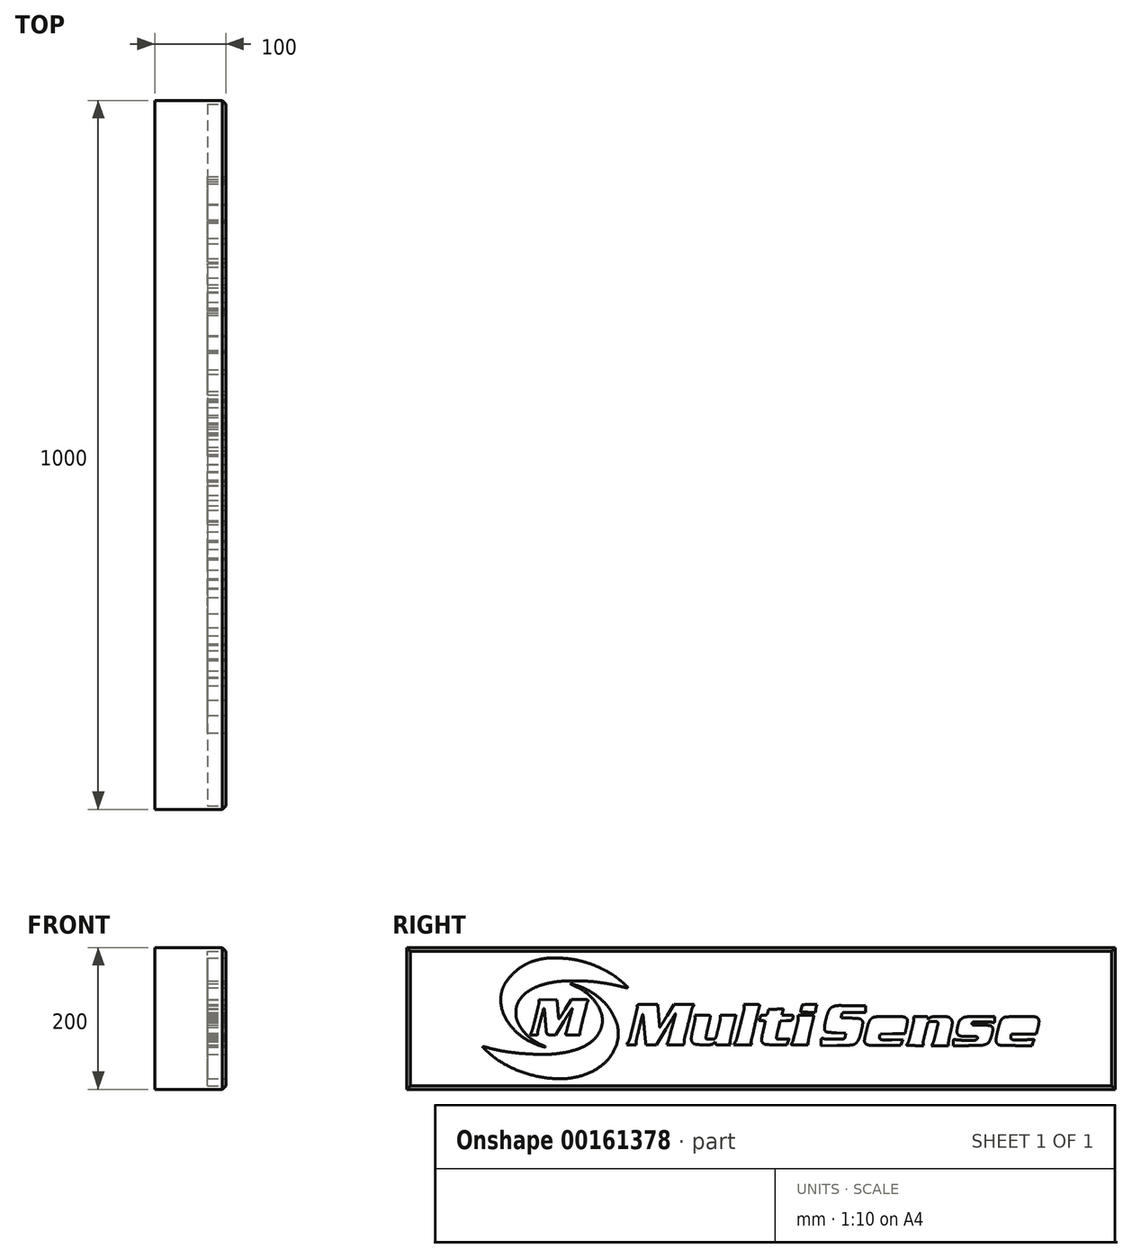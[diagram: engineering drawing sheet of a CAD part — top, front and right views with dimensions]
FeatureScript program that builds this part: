
annotation { "Feature Type Name" : "Feature", "Feature Type Description" : "" }
export const myFeature = defineFeature(function(context is Context, id is Id, definition is map)
    precondition{}
    {
        {
            var Q0;
            Q0=qCreatedBy(makeId("Right.planeOp"),FACE);
            var sketch = newSketch(context, id + "F0", { "sketchPlane" : qUnion([Q0])});
            skLineSegment(sketch, "E0.bottom", {"start": v(500, 100) * mm, "end": v(-500, 100) * mm});
            skLineSegment(sketch, "E0.top", {"start": v(500, -100) * mm, "end": v(-500, -100) * mm});
            skLineSegment(sketch, "E0.left", {"start": v(500, 100) * mm, "end": v(500, -100) * mm});
            skLineSegment(sketch, "E0.right", {"start": v(-500, 100) * mm, "end": v(-500, -100) * mm});
            skPoint(sketch, "E0.middle", {"position": v(0, 0) * mm});
            skSolve(sketch);
        }
        {
            var Q0;
            Q0=makeQuery(id+"F0.imprint","IMPRINT",FACE,{"disambiguationData":[TD([[makeQuery(id+"F0.imprint","IMPRINT",EDGE,{"derivedFrom":sQuery(id+"F0.wireOp",EDGE,"0kaTTqBf-60IO-ZrBU-QRsl-RT9rZZWctxwf")}),1.0]])]});
            var Q1;
            Q1=makeQuery(id+"F0.imprint","IMPRINT",FACE,{"disambiguationData":[TD([[makeQuery(id+"F0.imprint","IMPRINT",EDGE,{"derivedFrom":sQuery(id+"F0.wireOp",EDGE,"E0.bottom")}),1.0]])]});
            extrude(context, id + "F1", {"entities" : qUnion([Q0, Q1]), "depth" : 100 * mm});
        }
        {
            var Q0;
            Q0=makeQuery(id+"F1.opExtrude","CAP_EDGE",EDGE,{"disambiguationData":[OSD([sQuery(id+"F0.wireOp",EDGE,"E0.bottom")])],"isStart":false});
            var Q1;
            Q1=makeQuery(id+"F1.opExtrude","CAP_EDGE",EDGE,{"disambiguationData":[OSD([sQuery(id+"F0.wireOp",EDGE,"E0.right")])],"isStart":false});
            var Q2;
            Q2=makeQuery(id+"F1.opExtrude","CAP_EDGE",EDGE,{"disambiguationData":[OSD([sQuery(id+"F0.wireOp",EDGE,"E0.top")])],"isStart":false});
            var Q3;
            Q3=makeQuery(id+"F1.opExtrude","CAP_EDGE",EDGE,{"disambiguationData":[OSD([sQuery(id+"F0.wireOp",EDGE,"E0.left")])],"isStart":false});
            chamfer(context, id + "F2", {"entities" : qUnion([Q0, Q1, Q2, Q3]), "width" : 5 * mm, "tangentPropagation" : true});
        }
        {
            var Q0;
            Q0=makeQuery(id+"F1.opExtrude","CAP_FACE",FACE,{"disambiguationData":[OSD([sQuery(id+"F0.wireOp",EDGE,"E0.bottom"),sQuery(id+"F0.wireOp",EDGE,"E0.top"),sQuery(id+"F0.wireOp",EDGE,"E0.left"),sQuery(id+"F0.wireOp",EDGE,"E0.right")])],"isStart":false});
            var sketch = newSketch(context, id + "F3", { "sketchPlane" : qUnion([Q0])});
            skArc(sketch, "E1", {"start": v(-307.52, 84.22) * mm, "mid": v(-314, 82.86) * mm, "end": v(-320.37, 81.12) * mm});
            skArc(sketch, "E2", {"start": v(-320.37, 81.12) * mm, "mid": v(-325.97, 79.14) * mm, "end": v(-331.38, 76.7) * mm});
            skArc(sketch, "E3", {"start": v(-331.38, 76.7) * mm, "mid": v(-336.4, 73.9) * mm, "end": v(-341.16, 70.67) * mm});
            skArc(sketch, "E4", {"start": v(-341.16, 70.67) * mm, "mid": v(-345.91, 66.85) * mm, "end": v(-350.37, 62.7) * mm});
            skArc(sketch, "E5", {"start": v(-350.37, 62.7) * mm, "mid": v(-354.46, 58.31) * mm, "end": v(-358.25, 53.66) * mm});
            skArc(sketch, "E6", {"start": v(-358.25, 53.66) * mm, "mid": v(-361.09, 49.48) * mm, "end": v(-363.45, 45.02) * mm});
            skArc(sketch, "E7", {"start": v(-363.45, 45.02) * mm, "mid": v(-365.18, 40.59) * mm, "end": v(-366.36, 35.99) * mm});
            skArc(sketch, "E8", {"start": v(-366.36, 35.99) * mm, "mid": v(-367.1, 30.93) * mm, "end": v(-367.34, 25.82) * mm});
            skArc(sketch, "E9", {"start": v(-367.34, 25.82) * mm, "mid": v(-366.34, 15.86) * mm, "end": v(-363.36, 6.3) * mm});
            skArc(sketch, "E10", {"start": v(-363.36, 6.3) * mm, "mid": v(-358.3, -3.45) * mm, "end": v(-351.8, -12.3) * mm});
            skArc(sketch, "E11", {"start": v(-351.8, -12.3) * mm, "mid": v(-343.53, -20.68) * mm, "end": v(-334.15, -27.8) * mm});
            skArc(sketch, "E12", {"start": v(-334.15, -27.8) * mm, "mid": v(-323.61, -33.75) * mm, "end": v(-312.4, -38.27) * mm});
            skArc(sketch, "E13", {"start": v(-312.4, -38.27) * mm, "mid": v(-309.3, -39.26) * mm, "end": v(-306.21, -40.23) * mm});
            skArc(sketch, "E14", {"start": v(-306.21, -40.23) * mm, "mid": v(-305.4, -40.35) * mm, "end": v(-304.6, -40.24) * mm});
            skArc(sketch, "E15", {"start": v(-304.6, -40.24) * mm, "mid": v(-304.38, -39.97) * mm, "end": v(-304.56, -39.66) * mm});
            skArc(sketch, "E16", {"start": v(-304.56, -39.66) * mm, "mid": v(-307.06, -38.53) * mm, "end": v(-309.58, -37.43) * mm});
            skArc(sketch, "E17", {"start": v(-309.58, -37.43) * mm, "mid": v(-314.83, -34.92) * mm, "end": v(-319.85, -31.98) * mm});
            skArc(sketch, "E18", {"start": v(-319.85, -31.98) * mm, "mid": v(-324.6, -28.62) * mm, "end": v(-329.03, -24.87) * mm});
            skArc(sketch, "E19", {"start": v(-329.03, -24.87) * mm, "mid": v(-333.02, -20.86) * mm, "end": v(-336.64, -16.52) * mm});
            skArc(sketch, "E20", {"start": v(-336.64, -16.52) * mm, "mid": v(-339.67, -12.08) * mm, "end": v(-342.24, -7.36) * mm});
            skArc(sketch, "E21", {"start": v(-342.24, -7.36) * mm, "mid": v(-343.26, -5.14) * mm, "end": v(-344.23, -2.9) * mm});
            skArc(sketch, "E22", {"start": v(-344.23, -2.9) * mm, "mid": v(-344.8, -1.36) * mm, "end": v(-345.23, 0.22) * mm});
            skArc(sketch, "E23", {"start": v(-345.23, 0.22) * mm, "mid": v(-345.52, 1.81) * mm, "end": v(-345.68, 3.42) * mm});
            skArc(sketch, "E24", {"start": v(-345.68, 3.42) * mm, "mid": v(-345.78, 5.78) * mm, "end": v(-345.8, 8.14) * mm});
            skArc(sketch, "E25", {"start": v(-345.8, 8.14) * mm, "mid": v(-345.77, 10.33) * mm, "end": v(-345.68, 12.52) * mm});
            skArc(sketch, "E26", {"start": v(-345.68, 12.52) * mm, "mid": v(-345.53, 14.12) * mm, "end": v(-345.27, 15.7) * mm});
            skArc(sketch, "E27", {"start": v(-345.27, 15.7) * mm, "mid": v(-344.93, 17.16) * mm, "end": v(-344.48, 18.58) * mm});
            skArc(sketch, "E28", {"start": v(-344.48, 18.58) * mm, "mid": v(-343.83, 20.26) * mm, "end": v(-343.11, 21.9) * mm});
            skArc(sketch, "E29", {"start": v(-343.11, 21.9) * mm, "mid": v(-339.85, 27.54) * mm, "end": v(-335.6, 32.48) * mm});
            skArc(sketch, "E30", {"start": v(-335.6, 32.48) * mm, "mid": v(-330.08, 37.17) * mm, "end": v(-323.98, 41.1) * mm});
            skArc(sketch, "E31", {"start": v(-323.98, 41.1) * mm, "mid": v(-316.38, 44.76) * mm, "end": v(-308.41, 47.56) * mm});
            skArc(sketch, "E32", {"start": v(-308.41, 47.56) * mm, "mid": v(-298.85, 49.98) * mm, "end": v(-289.15, 51.72) * mm});
            skArc(sketch, "E33", {"start": v(-289.15, 51.72) * mm, "mid": v(-284.13, 52.3) * mm, "end": v(-279.1, 52.6) * mm});
            skArc(sketch, "E34", {"start": v(-279.1, 52.6) * mm, "mid": v(-271.29, 52.8) * mm, "end": v(-263.49, 52.86) * mm});
            skArc(sketch, "E35", {"start": v(-263.49, 52.86) * mm, "mid": v(-255.52, 52.8) * mm, "end": v(-247.55, 52.6) * mm});
            skArc(sketch, "E36", {"start": v(-247.55, 52.6) * mm, "mid": v(-241.69, 52.3) * mm, "end": v(-235.84, 51.75) * mm});
            skArc(sketch, "E37", {"start": v(-235.84, 51.75) * mm, "mid": v(-230.71, 51.13) * mm, "end": v(-225.6, 50.44) * mm});
            skArc(sketch, "E38", {"start": v(-225.6, 50.44) * mm, "mid": v(-220.73, 49.7) * mm, "end": v(-215.88, 48.9) * mm});
            skArc(sketch, "E39", {"start": v(-215.88, 48.9) * mm, "mid": v(-211.3, 48.06) * mm, "end": v(-206.75, 47.14) * mm});
            skArc(sketch, "E40", {"start": v(-206.75, 47.14) * mm, "mid": v(-202.48, 46.2) * mm, "end": v(-198.24, 45.16) * mm});
            skArc(sketch, "E41", {"start": v(-198.24, 45.16) * mm, "mid": v(-196.43, 44.72) * mm, "end": v(-194.61, 44.29) * mm});
            skArc(sketch, "E42", {"start": v(-194.61, 44.29) * mm, "mid": v(-193.05, 43.94) * mm, "end": v(-191.48, 43.62) * mm});
            skArc(sketch, "E43", {"start": v(-191.48, 43.62) * mm, "mid": v(-190.15, 43.36) * mm, "end": v(-188.82, 43.1) * mm});
            skArc(sketch, "E44", {"start": v(-188.82, 43.1) * mm, "mid": v(-188.6, 43.12) * mm, "end": v(-188.42, 43.23) * mm});
            skArc(sketch, "E45", {"start": v(-188.42, 43.23) * mm, "mid": v(-188.16, 43.87) * mm, "end": v(-188.44, 44.5) * mm});
            skArc(sketch, "E46", {"start": v(-188.44, 44.5) * mm, "mid": v(-191.8, 47.56) * mm, "end": v(-195.19, 50.58) * mm});
            skArc(sketch, "E47", {"start": v(-195.19, 50.58) * mm, "mid": v(-198.7, 53.6) * mm, "end": v(-202.29, 56.52) * mm});
            skArc(sketch, "E48", {"start": v(-202.29, 56.52) * mm, "mid": v(-205.37, 58.84) * mm, "end": v(-208.55, 61.01) * mm});
            skArc(sketch, "E49", {"start": v(-208.55, 61.01) * mm, "mid": v(-214.74, 64.83) * mm, "end": v(-221.1, 68.34) * mm});
            skArc(sketch, "E50", {"start": v(-221.1, 68.34) * mm, "mid": v(-227.55, 71.52) * mm, "end": v(-234.15, 74.38) * mm});
            skArc(sketch, "E51", {"start": v(-234.15, 74.38) * mm, "mid": v(-240.93, 76.94) * mm, "end": v(-247.82, 79.16) * mm});
            skArc(sketch, "E52", {"start": v(-247.82, 79.16) * mm, "mid": v(-254.97, 81.1) * mm, "end": v(-262.2, 82.72) * mm});
            skArc(sketch, "E53", {"start": v(-262.2, 82.72) * mm, "mid": v(-267.5, 83.65) * mm, "end": v(-272.86, 84.29) * mm});
            skArc(sketch, "E54", {"start": v(-272.86, 84.29) * mm, "mid": v(-279.34, 84.8) * mm, "end": v(-285.83, 85.1) * mm});
            skArc(sketch, "E55", {"start": v(-285.83, 85.1) * mm, "mid": v(-292.1, 85.22) * mm, "end": v(-298.39, 85.14) * mm});
            skArc(sketch, "E56", {"start": v(-298.39, 85.14) * mm, "mid": v(-302.97, 84.85) * mm, "end": v(-307.52, 84.22) * mm});
            skArc(sketch, "E57", {"start": v(-264.04, 46.2) * mm, "mid": v(-255, 41.77) * mm, "end": v(-246.62, 36.19) * mm});
            skArc(sketch, "E58", {"start": v(-246.62, 36.19) * mm, "mid": v(-239.35, 29.72) * mm, "end": v(-233.1, 22.27) * mm});
            skArc(sketch, "E59", {"start": v(-233.1, 22.27) * mm, "mid": v(-228.54, 14.74) * mm, "end": v(-225.26, 6.56) * mm});
            skArc(sketch, "E60", {"start": v(-225.26, 6.56) * mm, "mid": v(-223.9, -1) * mm, "end": v(-224.4, -8.69) * mm});
            skArc(sketch, "E61", {"start": v(-224.4, -8.69) * mm, "mid": v(-226.65, -16.2) * mm, "end": v(-230.41, -23.1) * mm});
            skArc(sketch, "E62", {"start": v(-230.41, -23.1) * mm, "mid": v(-235.7, -29.47) * mm, "end": v(-242.05, -34.8) * mm});
            skArc(sketch, "E63", {"start": v(-242.05, -34.8) * mm, "mid": v(-250.38, -39.77) * mm, "end": v(-259.33, -43.47) * mm});
            skArc(sketch, "E64", {"start": v(-259.33, -43.47) * mm, "mid": v(-270.52, -46.66) * mm, "end": v(-281.95, -48.9) * mm});
            skArc(sketch, "E65", {"start": v(-281.95, -48.9) * mm, "mid": v(-293.44, -50.22) * mm, "end": v(-305, -50.7) * mm});
            skArc(sketch, "E66", {"start": v(-305, -50.7) * mm, "mid": v(-319.29, -50.5) * mm, "end": v(-333.55, -49.74) * mm});
            skArc(sketch, "E67", {"start": v(-333.55, -49.74) * mm, "mid": v(-347.86, -48.4) * mm, "end": v(-362.12, -46.52) * mm});
            skArc(sketch, "E68", {"start": v(-362.12, -46.52) * mm, "mid": v(-373.8, -44.33) * mm, "end": v(-385.3, -41.35) * mm});
            skArc(sketch, "E69", {"start": v(-385.3, -41.35) * mm, "mid": v(-386.55, -40.99) * mm, "end": v(-387.8, -40.65) * mm});
            skArc(sketch, "E70", {"start": v(-387.8, -40.65) * mm, "mid": v(-388.9, -40.38) * mm, "end": v(-390, -40.14) * mm});
            skArc(sketch, "E71", {"start": v(-390, -40.14) * mm, "mid": v(-390.91, -39.96) * mm, "end": v(-391.83, -39.8) * mm});
            skArc(sketch, "E72", {"start": v(-391.83, -39.8) * mm, "mid": v(-392.06, -39.82) * mm, "end": v(-392.25, -39.93) * mm});
            skArc(sketch, "E73", {"start": v(-392.25, -39.93) * mm, "mid": v(-392.5, -40.54) * mm, "end": v(-392.23, -41.13) * mm});
            skArc(sketch, "E74", {"start": v(-392.23, -41.13) * mm, "mid": v(-388.73, -44.37) * mm, "end": v(-385.2, -47.58) * mm});
            skArc(sketch, "E75", {"start": v(-385.2, -47.58) * mm, "mid": v(-381.63, -50.73) * mm, "end": v(-377.98, -53.8) * mm});
            skArc(sketch, "E76", {"start": v(-377.98, -53.8) * mm, "mid": v(-374.96, -56.15) * mm, "end": v(-371.83, -58.37) * mm});
            skArc(sketch, "E77", {"start": v(-371.83, -58.37) * mm, "mid": v(-358.73, -66.27) * mm, "end": v(-344.89, -72.78) * mm});
            skArc(sketch, "E78", {"start": v(-344.89, -72.78) * mm, "mid": v(-330.02, -78.08) * mm, "end": v(-314.71, -81.97) * mm});
            skArc(sketch, "E79", {"start": v(-314.71, -81.97) * mm, "mid": v(-299.63, -84.32) * mm, "end": v(-284.4, -85.21) * mm});
            skArc(sketch, "E80", {"start": v(-284.4, -85.21) * mm, "mid": v(-270.61, -84.46) * mm, "end": v(-257.04, -81.94) * mm});
            skArc(sketch, "E81", {"start": v(-257.04, -81.94) * mm, "mid": v(-244.14, -77.62) * mm, "end": v(-232.02, -71.43) * mm});
            skArc(sketch, "E82", {"start": v(-232.02, -71.43) * mm, "mid": v(-221.84, -63.89) * mm, "end": v(-213.2, -54.6) * mm});
            skArc(sketch, "E83", {"start": v(-213.2, -54.6) * mm, "mid": v(-207.02, -44.64) * mm, "end": v(-202.98, -33.63) * mm});
            skArc(sketch, "E84", {"start": v(-202.98, -33.63) * mm, "mid": v(-201.43, -22.43) * mm, "end": v(-202.43, -11.16) * mm});
            skArc(sketch, "E85", {"start": v(-202.43, -11.16) * mm, "mid": v(-203.29, -7.77) * mm, "end": v(-204.46, -4.47) * mm});
            skArc(sketch, "E86", {"start": v(-204.46, -4.47) * mm, "mid": v(-206.3, -0.23) * mm, "end": v(-208.32, 3.92) * mm});
            skArc(sketch, "E87", {"start": v(-208.32, 3.92) * mm, "mid": v(-210.55, 8.08) * mm, "end": v(-212.96, 12.14) * mm});
            skArc(sketch, "E88", {"start": v(-212.96, 12.14) * mm, "mid": v(-215.12, 15.35) * mm, "end": v(-217.52, 18.39) * mm});
            skArc(sketch, "E89", {"start": v(-217.52, 18.39) * mm, "mid": v(-222, 23.25) * mm, "end": v(-226.81, 27.78) * mm});
            skArc(sketch, "E90", {"start": v(-226.81, 27.78) * mm, "mid": v(-231.98, 31.97) * mm, "end": v(-237.45, 35.77) * mm});
            skArc(sketch, "E91", {"start": v(-237.45, 35.77) * mm, "mid": v(-243.27, 39.23) * mm, "end": v(-249.33, 42.27) * mm});
            skArc(sketch, "E92", {"start": v(-249.33, 42.27) * mm, "mid": v(-255.76, 44.97) * mm, "end": v(-262.34, 47.23) * mm});
            skArc(sketch, "E93", {"start": v(-262.34, 47.23) * mm, "mid": v(-264.75, 47.96) * mm, "end": v(-267.17, 48.66) * mm});
            skArc(sketch, "E94", {"start": v(-267.17, 48.66) * mm, "mid": v(-267.72, 48.7) * mm, "end": v(-268.24, 48.52) * mm});
            skArc(sketch, "E95", {"start": v(-268.24, 48.52) * mm, "mid": v(-268.39, 48.24) * mm, "end": v(-268.2, 47.99) * mm});
            skArc(sketch, "E96", {"start": v(-268.2, 47.99) * mm, "mid": v(-266.13, 47.08) * mm, "end": v(-264.04, 46.2) * mm});
            skArc(sketch, "E97", {"start": v(-313.34, 23.63) * mm, "mid": v(-313.48, 21.37) * mm, "end": v(-313.87, 19.14) * mm});
            skArc(sketch, "E98", {"start": v(-313.87, 19.14) * mm, "mid": v(-315.82, 10.99) * mm, "end": v(-317.81, 2.84) * mm});
            skArc(sketch, "E99", {"start": v(-317.81, 2.84) * mm, "mid": v(-319.8, -5.08) * mm, "end": v(-321.82, -12.99) * mm});
            skArc(sketch, "E100", {"start": v(-321.82, -12.99) * mm, "mid": v(-322.75, -16.1) * mm, "end": v(-323.89, -19.12) * mm});
            skArc(sketch, "E101", {"start": v(-323.89, -19.12) * mm, "mid": v(-324.17, -19.8) * mm, "end": v(-324.45, -20.48) * mm});
            skArc(sketch, "E102", {"start": v(-324.45, -20.48) * mm, "mid": v(-324.68, -21.09) * mm, "end": v(-324.92, -21.7) * mm});
            skArc(sketch, "E103", {"start": v(-324.92, -21.7) * mm, "mid": v(-325.1, -22.2) * mm, "end": v(-325.3, -22.72) * mm});
            skArc(sketch, "E104", {"start": v(-325.3, -22.72) * mm, "mid": v(-325.33, -22.85) * mm, "end": v(-325.34, -22.98) * mm});
            skArc(sketch, "E105", {"start": v(-325.34, -22.98) * mm, "mid": v(-325.3, -23.09) * mm, "end": v(-325.2, -23.13) * mm});
            skArc(sketch, "E106", {"start": v(-325.2, -23.13) * mm, "mid": v(-324.49, -23.2) * mm, "end": v(-323.77, -23.25) * mm});
            skArc(sketch, "E107", {"start": v(-323.77, -23.25) * mm, "mid": v(-322.9, -23.3) * mm, "end": v(-322.04, -23.33) * mm});
            skArc(sketch, "E108", {"start": v(-322.04, -23.33) * mm, "mid": v(-321.01, -23.35) * mm, "end": v(-319.98, -23.36) * mm});
            skArc(sketch, "E109", {"start": v(-319.98, -23.36) * mm, "mid": v(-318.34, -23.35) * mm, "end": v(-316.7, -23.3) * mm});
            skArc(sketch, "E110", {"start": v(-316.7, -23.3) * mm, "mid": v(-316.08, -23.23) * mm, "end": v(-315.48, -23.02) * mm});
            skArc(sketch, "E111", {"start": v(-315.48, -23.02) * mm, "mid": v(-315.15, -22.76) * mm, "end": v(-314.99, -22.37) * mm});
            skArc(sketch, "E112", {"start": v(-314.99, -22.37) * mm, "mid": v(-314.94, -21.74) * mm, "end": v(-315, -21.11) * mm});
            skArc(sketch, "E113", {"start": v(-315, -21.11) * mm, "mid": v(-315.12, -19.27) * mm, "end": v(-314.86, -17.44) * mm});
            skArc(sketch, "E114", {"start": v(-314.86, -17.44) * mm, "mid": v(-312.92, -9.67) * mm, "end": v(-310.94, -1.9) * mm});
            skArc(sketch, "E115", {"start": v(-310.94, -1.9) * mm, "mid": v(-308.92, 5.86) * mm, "end": v(-306.86, 13.62) * mm});
            skArc(sketch, "E116", {"start": v(-306.86, 13.62) * mm, "mid": v(-306.45, 13.94) * mm, "end": v(-306.02, 13.64) * mm});
            skArc(sketch, "E117", {"start": v(-306.02, 13.64) * mm, "mid": v(-305.88, 13.1) * mm, "end": v(-305.79, 12.55) * mm});
            skArc(sketch, "E118", {"start": v(-305.79, 12.55) * mm, "mid": v(-305.56, 10.36) * mm, "end": v(-305.34, 8.17) * mm});
            skArc(sketch, "E119", {"start": v(-305.34, 8.17) * mm, "mid": v(-305.1, 5.59) * mm, "end": v(-304.86, 3) * mm});
            skArc(sketch, "E120", {"start": v(-304.86, 3) * mm, "mid": v(-304.62, 0.07) * mm, "end": v(-304.39, -2.86) * mm});
            skArc(sketch, "E121", {"start": v(-304.39, -2.86) * mm, "mid": v(-303.8, -10.36) * mm, "end": v(-303.18, -17.85) * mm});
            skArc(sketch, "E122", {"start": v(-303.18, -17.85) * mm, "mid": v(-302.9, -19.65) * mm, "end": v(-302.33, -21.4) * mm});
            skArc(sketch, "E123", {"start": v(-302.33, -21.4) * mm, "mid": v(-301.6, -22.39) * mm, "end": v(-300.47, -22.92) * mm});
            skArc(sketch, "E124", {"start": v(-300.47, -22.92) * mm, "mid": v(-298.26, -23.25) * mm, "end": v(-296.01, -23.35) * mm});
            skLineSegment(sketch, "E125", {"start": v(-296.01, -23.35) * mm, "end": v(-289.84, -23.35) * mm});
            skLineSegment(sketch, "E126", {"start": v(-289.84, -23.35) * mm, "end": v(-278.36, -4.32) * mm});
            skArc(sketch, "E127", {"start": v(-278.36, -4.32) * mm, "mid": v(-276.15, -0.7) * mm, "end": v(-273.93, 2.92) * mm});
            skArc(sketch, "E128", {"start": v(-273.93, 2.92) * mm, "mid": v(-272.06, 5.91) * mm, "end": v(-270.17, 8.89) * mm});
            skArc(sketch, "E129", {"start": v(-270.17, 8.89) * mm, "mid": v(-268.53, 11.43) * mm, "end": v(-266.9, 13.96) * mm});
            skArc(sketch, "E130", {"start": v(-266.9, 13.96) * mm, "mid": v(-266.74, 14.03) * mm, "end": v(-266.62, 13.92) * mm});
            skArc(sketch, "E131", {"start": v(-266.62, 13.92) * mm, "mid": v(-266.52, 13.29) * mm, "end": v(-266.59, 12.65) * mm});
            skArc(sketch, "E132", {"start": v(-266.59, 12.65) * mm, "mid": v(-268.61, 4.75) * mm, "end": v(-270.65, -3.15) * mm});
            skArc(sketch, "E133", {"start": v(-270.65, -3.15) * mm, "mid": v(-272.57, -10.57) * mm, "end": v(-274.51, -17.98) * mm});
            skArc(sketch, "E134", {"start": v(-274.51, -17.98) * mm, "mid": v(-275.08, -19.82) * mm, "end": v(-275.78, -21.61) * mm});
            skArc(sketch, "E135", {"start": v(-275.78, -21.61) * mm, "mid": v(-275.86, -22.08) * mm, "end": v(-275.68, -22.53) * mm});
            skArc(sketch, "E136", {"start": v(-275.68, -22.53) * mm, "mid": v(-275.29, -22.9) * mm, "end": v(-274.78, -23.09) * mm});
            skArc(sketch, "E137", {"start": v(-274.78, -23.09) * mm, "mid": v(-273.57, -23.25) * mm, "end": v(-272.35, -23.32) * mm});
            skArc(sketch, "E138", {"start": v(-272.35, -23.32) * mm, "mid": v(-269.15, -23.35) * mm, "end": v(-265.95, -23.36) * mm});
            skLineSegment(sketch, "E139", {"start": v(-265.95, -23.36) * mm, "end": v(-255.34, -23.36) * mm});
            skLineSegment(sketch, "E140", {"start": v(-255.34, -23.36) * mm, "end": v(-255.34, -20.32) * mm});
            skArc(sketch, "E141", {"start": v(-255.34, -20.32) * mm, "mid": v(-255.2, -17.9) * mm, "end": v(-254.77, -15.5) * mm});
            skArc(sketch, "E142", {"start": v(-254.77, -15.5) * mm, "mid": v(-252.55, -6.33) * mm, "end": v(-250.29, 2.83) * mm});
            skArc(sketch, "E143", {"start": v(-250.29, 2.83) * mm, "mid": v(-247.9, 12.4) * mm, "end": v(-245.48, 21.96) * mm});
            skArc(sketch, "E144", {"start": v(-245.48, 21.96) * mm, "mid": v(-245.02, 23.1) * mm, "end": v(-244.28, 24.09) * mm});
            skArc(sketch, "E145", {"start": v(-244.28, 24.09) * mm, "mid": v(-243.95, 24.66) * mm, "end": v(-243.92, 25.32) * mm});
            skArc(sketch, "E146", {"start": v(-243.92, 25.32) * mm, "mid": v(-244.22, 25.87) * mm, "end": v(-244.76, 26.17) * mm});
            skArc(sketch, "E147", {"start": v(-244.76, 26.17) * mm, "mid": v(-246.35, 26.45) * mm, "end": v(-247.96, 26.56) * mm});
            skArc(sketch, "E148", {"start": v(-247.96, 26.56) * mm, "mid": v(-251.78, 26.62) * mm, "end": v(-255.6, 26.64) * mm});
            skLineSegment(sketch, "E149", {"start": v(-255.6, 26.64) * mm, "end": v(-267.84, 26.63) * mm});
            skLineSegment(sketch, "E150", {"start": v(-267.84, 26.63) * mm, "end": v(-276.34, 12.74) * mm});
            skArc(sketch, "E151", {"start": v(-276.34, 12.74) * mm, "mid": v(-277.98, 10.08) * mm, "end": v(-279.63, 7.44) * mm});
            skArc(sketch, "E152", {"start": v(-279.63, 7.44) * mm, "mid": v(-281.04, 5.23) * mm, "end": v(-282.47, 3.04) * mm});
            skArc(sketch, "E153", {"start": v(-282.47, 3.04) * mm, "mid": v(-283.72, 1.17) * mm, "end": v(-284.98, -0.71) * mm});
            skArc(sketch, "E154", {"start": v(-284.98, -0.71) * mm, "mid": v(-285.12, -0.8) * mm, "end": v(-285.28, -0.74) * mm});
            skArc(sketch, "E155", {"start": v(-285.28, -0.74) * mm, "mid": v(-285.41, -0.56) * mm, "end": v(-285.47, -0.35) * mm});
            skArc(sketch, "E156", {"start": v(-285.47, -0.35) * mm, "mid": v(-285.69, 1.55) * mm, "end": v(-285.9, 3.44) * mm});
            skArc(sketch, "E157", {"start": v(-285.9, 3.44) * mm, "mid": v(-286.13, 5.62) * mm, "end": v(-286.34, 7.8) * mm});
            skArc(sketch, "E158", {"start": v(-286.34, 7.8) * mm, "mid": v(-286.57, 10.36) * mm, "end": v(-286.78, 12.9) * mm});
            skLineSegment(sketch, "E159", {"start": v(-286.78, 12.9) * mm, "end": v(-287.84, 26.14) * mm});
            skLineSegment(sketch, "E160", {"start": v(-287.84, 26.14) * mm, "end": v(-300.6, 26.42) * mm});
            skLineSegment(sketch, "E161", {"start": v(-300.6, 26.42) * mm, "end": v(-313.34, 26.7) * mm});
            skLineSegment(sketch, "E162", {"start": v(-313.34, 26.7) * mm, "end": v(-313.34, 23.63) * mm});
            skArc(sketch, "E163", {"start": v(-174.84, 17.62) * mm, "mid": v(-174.53, 15.85) * mm, "end": v(-174.7, 14.07) * mm});
            skArc(sketch, "E164", {"start": v(-174.7, 14.07) * mm, "mid": v(-177.27, 3.25) * mm, "end": v(-179.88, -7.56) * mm});
            skArc(sketch, "E165", {"start": v(-179.88, -7.56) * mm, "mid": v(-182.44, -17.93) * mm, "end": v(-185.06, -28.28) * mm});
            skArc(sketch, "E166", {"start": v(-185.06, -28.28) * mm, "mid": v(-186.05, -31.27) * mm, "end": v(-187.42, -34.11) * mm});
            skLineSegment(sketch, "E167", {"start": v(-187.42, -34.11) * mm, "end": v(-189.28, -37.36) * mm});
            skLineSegment(sketch, "E168", {"start": v(-189.28, -37.36) * mm, "end": v(-182.81, -37.36) * mm});
            skLineSegment(sketch, "E169", {"start": v(-182.81, -37.36) * mm, "end": v(-176.34, -37.36) * mm});
            skLineSegment(sketch, "E170", {"start": v(-176.34, -37.36) * mm, "end": v(-176.34, -34.34) * mm});
            skArc(sketch, "E171", {"start": v(-176.34, -34.34) * mm, "mid": v(-176.23, -32.33) * mm, "end": v(-175.88, -30.34) * mm});
            skArc(sketch, "E172", {"start": v(-175.88, -30.34) * mm, "mid": v(-173.84, -21.72) * mm, "end": v(-171.77, -13.1) * mm});
            skArc(sketch, "E173", {"start": v(-171.77, -13.1) * mm, "mid": v(-169.55, -3.94) * mm, "end": v(-167.33, 5.21) * mm});
            skArc(sketch, "E174", {"start": v(-167.33, 5.21) * mm, "mid": v(-167.08, 5.46) * mm, "end": v(-166.75, 5.38) * mm});
            skArc(sketch, "E175", {"start": v(-166.75, 5.38) * mm, "mid": v(-166.64, 5.23) * mm, "end": v(-166.6, 5.06) * mm});
            skArc(sketch, "E176", {"start": v(-166.6, 5.06) * mm, "mid": v(-166.32, 2.46) * mm, "end": v(-166.05, -0.13) * mm});
            skArc(sketch, "E177", {"start": v(-166.05, -0.13) * mm, "mid": v(-165.75, -3.07) * mm, "end": v(-165.47, -6) * mm});
            skArc(sketch, "E178", {"start": v(-165.47, -6) * mm, "mid": v(-165.15, -9.46) * mm, "end": v(-164.84, -12.9) * mm});
            skArc(sketch, "E179", {"start": v(-164.84, -12.9) * mm, "mid": v(-164.53, -16.47) * mm, "end": v(-164.2, -20.02) * mm});
            skArc(sketch, "E180", {"start": v(-164.2, -20.02) * mm, "mid": v(-163.9, -23.28) * mm, "end": v(-163.58, -26.54) * mm});
            skArc(sketch, "E181", {"start": v(-163.58, -26.54) * mm, "mid": v(-163.31, -29.27) * mm, "end": v(-163.03, -32) * mm});
            skArc(sketch, "E182", {"start": v(-163.03, -32) * mm, "mid": v(-162.91, -33.06) * mm, "end": v(-162.76, -34.11) * mm});
            skLineSegment(sketch, "E183", {"start": v(-162.76, -34.11) * mm, "end": v(-162.25, -37.36) * mm});
            skLineSegment(sketch, "E184", {"start": v(-162.25, -37.36) * mm, "end": v(-154.98, -37.36) * mm});
            skLineSegment(sketch, "E185", {"start": v(-154.98, -37.36) * mm, "end": v(-147.7, -37.36) * mm});
            skLineSegment(sketch, "E186", {"start": v(-147.7, -37.36) * mm, "end": v(-134.46, -15.36) * mm});
            skArc(sketch, "E187", {"start": v(-134.46, -15.36) * mm, "mid": v(-131.91, -11.14) * mm, "end": v(-129.36, -6.92) * mm});
            skArc(sketch, "E188", {"start": v(-129.36, -6.92) * mm, "mid": v(-127.19, -3.37) * mm, "end": v(-125.01, 0.18) * mm});
            skArc(sketch, "E189", {"start": v(-125.01, 0.18) * mm, "mid": v(-123.05, 3.36) * mm, "end": v(-121.1, 6.54) * mm});
            skArc(sketch, "E190", {"start": v(-121.1, 6.54) * mm, "mid": v(-121.02, 6.61) * mm, "end": v(-120.91, 6.64) * mm});
            skArc(sketch, "E191", {"start": v(-120.91, 6.64) * mm, "mid": v(-120.63, 6.5) * mm, "end": v(-120.57, 6.2) * mm});
            skArc(sketch, "E192", {"start": v(-120.57, 6.2) * mm, "mid": v(-123.07, -3.2) * mm, "end": v(-125.57, -12.58) * mm});
            skArc(sketch, "E193", {"start": v(-125.57, -12.58) * mm, "mid": v(-127.9, -21.28) * mm, "end": v(-130.27, -29.97) * mm});
            skArc(sketch, "E194", {"start": v(-130.27, -29.97) * mm, "mid": v(-130.94, -32.08) * mm, "end": v(-131.79, -34.11) * mm});
            skLineSegment(sketch, "E195", {"start": v(-131.79, -34.11) * mm, "end": v(-133.31, -37.36) * mm});
            skLineSegment(sketch, "E196", {"start": v(-133.31, -37.36) * mm, "end": v(-120.95, -37.36) * mm});
            skLineSegment(sketch, "E197", {"start": v(-120.95, -37.36) * mm, "end": v(-108.58, -37.36) * mm});
            skLineSegment(sketch, "E198", {"start": v(-108.58, -37.36) * mm, "end": v(-108.53, -33.59) * mm});
            skArc(sketch, "E199", {"start": v(-108.53, -33.59) * mm, "mid": v(-108.32, -30.53) * mm, "end": v(-107.77, -27.5) * mm});
            skArc(sketch, "E200", {"start": v(-107.77, -27.5) * mm, "mid": v(-105.32, -17.42) * mm, "end": v(-102.83, -7.35) * mm});
            skArc(sketch, "E201", {"start": v(-102.83, -7.35) * mm, "mid": v(-100.23, 2.94) * mm, "end": v(-97.6, 13.23) * mm});
            skArc(sketch, "E202", {"start": v(-97.6, 13.23) * mm, "mid": v(-96.84, 15.38) * mm, "end": v(-95.76, 17.39) * mm});
            skLineSegment(sketch, "E203", {"start": v(-95.76, 17.39) * mm, "end": v(-94.3, 19.64) * mm});
            skLineSegment(sketch, "E204", {"start": v(-94.3, 19.64) * mm, "end": v(-108.57, 19.63) * mm});
            skLineSegment(sketch, "E205", {"start": v(-108.57, 19.63) * mm, "end": v(-122.84, 19.63) * mm});
            skLineSegment(sketch, "E206", {"start": v(-122.84, 19.63) * mm, "end": v(-132.68, 3.63) * mm});
            skArc(sketch, "E207", {"start": v(-132.68, 3.63) * mm, "mid": v(-134.57, 0.56) * mm, "end": v(-136.47, -2.5) * mm});
            skArc(sketch, "E208", {"start": v(-136.47, -2.5) * mm, "mid": v(-138.08, -5.08) * mm, "end": v(-139.7, -7.66) * mm});
            skArc(sketch, "E209", {"start": v(-139.7, -7.66) * mm, "mid": v(-141.16, -9.96) * mm, "end": v(-142.62, -12.26) * mm});
            skArc(sketch, "E210", {"start": v(-142.62, -12.26) * mm, "mid": v(-142.7, -12.33) * mm, "end": v(-142.8, -12.36) * mm});
            skArc(sketch, "E211", {"start": v(-142.8, -12.36) * mm, "mid": v(-142.88, -12.33) * mm, "end": v(-142.92, -12.25) * mm});
            skArc(sketch, "E212", {"start": v(-142.92, -12.25) * mm, "mid": v(-143.14, -9.95) * mm, "end": v(-143.37, -7.66) * mm});
            skArc(sketch, "E213", {"start": v(-143.37, -7.66) * mm, "mid": v(-143.6, -5.08) * mm, "end": v(-143.84, -2.5) * mm});
            skArc(sketch, "E214", {"start": v(-143.84, -2.5) * mm, "mid": v(-144.1, 0.57) * mm, "end": v(-144.34, 3.64) * mm});
            skLineSegment(sketch, "E215", {"start": v(-144.34, 3.64) * mm, "end": v(-145.6, 19.64) * mm});
            skLineSegment(sketch, "E216", {"start": v(-145.6, 19.64) * mm, "end": v(-160.54, 19.64) * mm});
            skArc(sketch, "E217", {"start": v(-160.54, 19.64) * mm, "mid": v(-165.38, 19.63) * mm, "end": v(-170.21, 19.6) * mm});
            skArc(sketch, "E218", {"start": v(-170.21, 19.6) * mm, "mid": v(-171.8, 19.54) * mm, "end": v(-173.38, 19.37) * mm});
            skArc(sketch, "E219", {"start": v(-173.38, 19.37) * mm, "mid": v(-174.04, 19.15) * mm, "end": v(-174.59, 18.73) * mm});
            skArc(sketch, "E220", {"start": v(-174.59, 18.73) * mm, "mid": v(-174.86, 18.2) * mm, "end": v(-174.84, 17.62) * mm});
            skArc(sketch, "E221", {"start": v(-23.8, 17.34) * mm, "mid": v(-23.56, 15.41) * mm, "end": v(-23.78, 13.48) * mm});
            skArc(sketch, "E222", {"start": v(-23.78, 13.48) * mm, "mid": v(-26.24, 3.1) * mm, "end": v(-28.75, -7.27) * mm});
            skArc(sketch, "E223", {"start": v(-28.75, -7.27) * mm, "mid": v(-31.2, -17.18) * mm, "end": v(-33.73, -27.07) * mm});
            skArc(sketch, "E224", {"start": v(-33.73, -27.07) * mm, "mid": v(-34.8, -30.4) * mm, "end": v(-36.24, -33.61) * mm});
            skLineSegment(sketch, "E225", {"start": v(-36.24, -33.61) * mm, "end": v(-38.18, -37.36) * mm});
            skLineSegment(sketch, "E226", {"start": v(-38.18, -37.36) * mm, "end": v(-25.74, -37.36) * mm});
            skLineSegment(sketch, "E227", {"start": v(-25.74, -37.36) * mm, "end": v(-13.3, -37.36) * mm});
            skLineSegment(sketch, "E228", {"start": v(-13.3, -37.36) * mm, "end": v(-13.88, -35.06) * mm});
            skArc(sketch, "E229", {"start": v(-13.88, -35.06) * mm, "mid": v(-14.04, -33.83) * mm, "end": v(-13.91, -32.59) * mm});
            skArc(sketch, "E230", {"start": v(-13.91, -32.59) * mm, "mid": v(-11.62, -22.49) * mm, "end": v(-9.32, -12.4) * mm});
            skArc(sketch, "E231", {"start": v(-9.32, -12.4) * mm, "mid": v(-7.14, -3.06) * mm, "end": v(-4.9, 6.26) * mm});
            skArc(sketch, "E232", {"start": v(-4.9, 6.26) * mm, "mid": v(-3.4, 12.1) * mm, "end": v(-1.73, 17.89) * mm});
            skArc(sketch, "E233", {"start": v(-1.73, 17.89) * mm, "mid": v(-1.73, 18.4) * mm, "end": v(-2, 18.82) * mm});
            skArc(sketch, "E234", {"start": v(-2, 18.82) * mm, "mid": v(-2.52, 19.17) * mm, "end": v(-3.12, 19.36) * mm});
            skArc(sketch, "E235", {"start": v(-3.12, 19.36) * mm, "mid": v(-4.48, 19.53) * mm, "end": v(-5.86, 19.6) * mm});
            skArc(sketch, "E236", {"start": v(-5.86, 19.6) * mm, "mid": v(-9.33, 19.63) * mm, "end": v(-12.8, 19.64) * mm});
            skLineSegment(sketch, "E237", {"start": v(-12.8, 19.64) * mm, "end": v(-24.38, 19.64) * mm});
            skLineSegment(sketch, "E238", {"start": v(-24.38, 19.64) * mm, "end": v(-23.8, 17.34) * mm});
            skArc(sketch, "E239", {"start": v(58.35, 18.89) * mm, "mid": v(58.24, 18.66) * mm, "end": v(58.15, 18.43) * mm});
            skArc(sketch, "E240", {"start": v(58.15, 18.43) * mm, "mid": v(58, 17.96) * mm, "end": v(57.85, 17.48) * mm});
            skArc(sketch, "E241", {"start": v(57.85, 17.48) * mm, "mid": v(57.7, 16.91) * mm, "end": v(57.54, 16.34) * mm});
            skArc(sketch, "E242", {"start": v(57.54, 16.34) * mm, "mid": v(57.39, 15.74) * mm, "end": v(57.25, 15.14) * mm});
            skArc(sketch, "E243", {"start": v(57.25, 15.14) * mm, "mid": v(57.1, 14.5) * mm, "end": v(56.95, 13.86) * mm});
            skArc(sketch, "E244", {"start": v(56.95, 13.86) * mm, "mid": v(56.78, 13.18) * mm, "end": v(56.6, 12.5) * mm});
            skArc(sketch, "E245", {"start": v(56.6, 12.5) * mm, "mid": v(56.45, 11.89) * mm, "end": v(56.29, 11.27) * mm});
            skArc(sketch, "E246", {"start": v(56.29, 11.27) * mm, "mid": v(56.17, 10.83) * mm, "end": v(56.04, 10.39) * mm});
            skArc(sketch, "E247", {"start": v(56.04, 10.39) * mm, "mid": v(56.03, 9.9) * mm, "end": v(56.26, 9.47) * mm});
            skArc(sketch, "E248", {"start": v(56.26, 9.47) * mm, "mid": v(56.72, 9.11) * mm, "end": v(57.27, 8.92) * mm});
            skArc(sketch, "E249", {"start": v(57.27, 8.92) * mm, "mid": v(58.5, 8.75) * mm, "end": v(59.75, 8.68) * mm});
            skArc(sketch, "E250", {"start": v(59.75, 8.68) * mm, "mid": v(62.85, 8.65) * mm, "end": v(65.96, 8.64) * mm});
            skLineSegment(sketch, "E251", {"start": v(65.96, 8.64) * mm, "end": v(76.4, 8.64) * mm});
            skLineSegment(sketch, "E252", {"start": v(76.4, 8.64) * mm, "end": v(76.98, 11.52) * mm});
            skArc(sketch, "E253", {"start": v(76.98, 11.52) * mm, "mid": v(77.11, 12.17) * mm, "end": v(77.25, 12.82) * mm});
            skArc(sketch, "E254", {"start": v(77.25, 12.82) * mm, "mid": v(77.42, 13.57) * mm, "end": v(77.58, 14.33) * mm});
            skArc(sketch, "E255", {"start": v(77.58, 14.33) * mm, "mid": v(77.75, 15.07) * mm, "end": v(77.92, 15.81) * mm});
            skArc(sketch, "E256", {"start": v(77.92, 15.81) * mm, "mid": v(78.07, 16.42) * mm, "end": v(78.22, 17.02) * mm});
            skLineSegment(sketch, "E257", {"start": v(78.22, 17.02) * mm, "end": v(78.87, 19.64) * mm});
            skLineSegment(sketch, "E258", {"start": v(78.87, 19.64) * mm, "end": v(68.82, 19.64) * mm});
            skArc(sketch, "E259", {"start": v(68.82, 19.64) * mm, "mid": v(66.88, 19.63) * mm, "end": v(64.94, 19.59) * mm});
            skArc(sketch, "E260", {"start": v(64.94, 19.59) * mm, "mid": v(63.27, 19.52) * mm, "end": v(61.6, 19.42) * mm});
            skArc(sketch, "E261", {"start": v(61.6, 19.42) * mm, "mid": v(60.2, 19.31) * mm, "end": v(58.82, 19.2) * mm});
            skArc(sketch, "E262", {"start": v(58.82, 19.2) * mm, "mid": v(58.55, 19.1) * mm, "end": v(58.35, 18.89) * mm});
            skArc(sketch, "E263", {"start": v(105.66, 17.76) * mm, "mid": v(103.04, 17.04) * mm, "end": v(100.53, 16.01) * mm});
            skArc(sketch, "E264", {"start": v(100.53, 16.01) * mm, "mid": v(98.71, 14.87) * mm, "end": v(97.2, 13.34) * mm});
            skArc(sketch, "E265", {"start": v(97.2, 13.34) * mm, "mid": v(95.78, 11.17) * mm, "end": v(94.73, 8.8) * mm});
            skArc(sketch, "E266", {"start": v(94.73, 8.8) * mm, "mid": v(93.36, 4.62) * mm, "end": v(92.14, 0.4) * mm});
            skArc(sketch, "E267", {"start": v(92.14, 0.4) * mm, "mid": v(91.22, -3.26) * mm, "end": v(90.41, -6.95) * mm});
            skArc(sketch, "E268", {"start": v(90.41, -6.95) * mm, "mid": v(89.97, -9.67) * mm, "end": v(89.74, -12.4) * mm});
            skArc(sketch, "E269", {"start": v(89.74, -12.4) * mm, "mid": v(89.77, -14.34) * mm, "end": v(90.01, -16.27) * mm});
            skArc(sketch, "E270", {"start": v(90.01, -16.27) * mm, "mid": v(90.46, -17.5) * mm, "end": v(91.3, -18.49) * mm});
            skArc(sketch, "E271", {"start": v(91.3, -18.49) * mm, "mid": v(91.97, -18.9) * mm, "end": v(92.7, -19.15) * mm});
            skArc(sketch, "E272", {"start": v(92.7, -19.15) * mm, "mid": v(94.22, -19.42) * mm, "end": v(95.74, -19.62) * mm});
            skArc(sketch, "E273", {"start": v(95.74, -19.62) * mm, "mid": v(97.92, -19.83) * mm, "end": v(100.1, -19.98) * mm});
            skArc(sketch, "E274", {"start": v(100.1, -19.98) * mm, "mid": v(103.27, -20.11) * mm, "end": v(106.42, -20.21) * mm});
            skLineSegment(sketch, "E275", {"start": v(106.42, -20.21) * mm, "end": v(119.88, -20.56) * mm});
            skLineSegment(sketch, "E276", {"start": v(119.88, -20.56) * mm, "end": v(119.3, -24.13) * mm});
            skArc(sketch, "E277", {"start": v(119.3, -24.13) * mm, "mid": v(119.17, -24.85) * mm, "end": v(118.99, -25.56) * mm});
            skArc(sketch, "E278", {"start": v(118.99, -25.56) * mm, "mid": v(118.78, -26.23) * mm, "end": v(118.52, -26.89) * mm});
            skArc(sketch, "E279", {"start": v(118.52, -26.89) * mm, "mid": v(118.27, -27.44) * mm, "end": v(117.98, -27.96) * mm});
            skArc(sketch, "E280", {"start": v(117.98, -27.96) * mm, "mid": v(117.74, -28.27) * mm, "end": v(117.44, -28.51) * mm});
            skArc(sketch, "E281", {"start": v(117.44, -28.51) * mm, "mid": v(116.22, -29.07) * mm, "end": v(114.9, -29.27) * mm});
            skArc(sketch, "E282", {"start": v(114.9, -29.27) * mm, "mid": v(109.12, -29.32) * mm, "end": v(103.34, -29.32) * mm});
            skArc(sketch, "E283", {"start": v(103.34, -29.32) * mm, "mid": v(97.72, -29.27) * mm, "end": v(92.1, -29.16) * mm});
            skArc(sketch, "E284", {"start": v(92.1, -29.16) * mm, "mid": v(90.17, -28.95) * mm, "end": v(88.3, -28.42) * mm});
            skArc(sketch, "E285", {"start": v(88.3, -28.42) * mm, "mid": v(87.41, -28.18) * mm, "end": v(86.5, -28.12) * mm});
            skArc(sketch, "E286", {"start": v(86.5, -28.12) * mm, "mid": v(85.85, -28.3) * mm, "end": v(85.38, -28.78) * mm});
            skArc(sketch, "E287", {"start": v(85.38, -28.78) * mm, "mid": v(84.98, -29.67) * mm, "end": v(84.8, -30.62) * mm});
            skArc(sketch, "E288", {"start": v(84.8, -30.62) * mm, "mid": v(84.7, -32.56) * mm, "end": v(84.66, -34.5) * mm});
            skLineSegment(sketch, "E289", {"start": v(84.66, -34.5) * mm, "end": v(84.66, -38.5) * mm});
            skLineSegment(sketch, "E290", {"start": v(84.66, -38.5) * mm, "end": v(107.4, -38.18) * mm});
            skArc(sketch, "E291", {"start": v(107.4, -38.18) * mm, "mid": v(114.06, -38.07) * mm, "end": v(120.7, -37.94) * mm});
            skArc(sketch, "E292", {"start": v(120.7, -37.94) * mm, "mid": v(123.8, -37.82) * mm, "end": v(126.89, -37.6) * mm});
            skArc(sketch, "E293", {"start": v(126.89, -37.6) * mm, "mid": v(128.72, -37.38) * mm, "end": v(130.53, -37.02) * mm});
            skArc(sketch, "E294", {"start": v(130.53, -37.02) * mm, "mid": v(131.8, -36.6) * mm, "end": v(132.96, -35.96) * mm});
            skArc(sketch, "E295", {"start": v(132.96, -35.96) * mm, "mid": v(134.38, -34.82) * mm, "end": v(135.6, -33.46) * mm});
            skArc(sketch, "E296", {"start": v(135.6, -33.46) * mm, "mid": v(136.8, -31.7) * mm, "end": v(137.82, -29.81) * mm});
            skArc(sketch, "E297", {"start": v(137.82, -29.81) * mm, "mid": v(138.9, -27.32) * mm, "end": v(139.8, -24.75) * mm});
            skArc(sketch, "E298", {"start": v(139.8, -24.75) * mm, "mid": v(140.79, -21.32) * mm, "end": v(141.66, -17.86) * mm});
            skArc(sketch, "E299", {"start": v(141.66, -17.86) * mm, "mid": v(142.8, -12.44) * mm, "end": v(143.7, -6.97) * mm});
            skArc(sketch, "E300", {"start": v(143.7, -6.97) * mm, "mid": v(143.54, -4.61) * mm, "end": v(142.45, -2.52) * mm});
            skArc(sketch, "E301", {"start": v(142.45, -2.52) * mm, "mid": v(140.58, -0.99) * mm, "end": v(138.27, -0.28) * mm});
            skArc(sketch, "E302", {"start": v(138.27, -0.28) * mm, "mid": v(132.42, 0.22) * mm, "end": v(126.55, 0.5) * mm});
            skLineSegment(sketch, "E303", {"start": v(126.55, 0.5) * mm, "end": v(113.66, 0.84) * mm});
            skLineSegment(sketch, "E304", {"start": v(113.66, 0.84) * mm, "end": v(113.67, 3.5) * mm});
            skArc(sketch, "E305", {"start": v(113.67, 3.5) * mm, "mid": v(113.84, 5.05) * mm, "end": v(114.32, 6.54) * mm});
            skArc(sketch, "E306", {"start": v(114.32, 6.54) * mm, "mid": v(115.02, 7.5) * mm, "end": v(116.07, 8.06) * mm});
            skArc(sketch, "E307", {"start": v(116.07, 8.06) * mm, "mid": v(118, 8.46) * mm, "end": v(119.98, 8.59) * mm});
            skArc(sketch, "E308", {"start": v(119.98, 8.59) * mm, "mid": v(125.74, 8.55) * mm, "end": v(131.51, 8.46) * mm});
            skLineSegment(sketch, "E309", {"start": v(131.51, 8.46) * mm, "end": v(147.66, 8.14) * mm});
            skLineSegment(sketch, "E310", {"start": v(147.66, 8.14) * mm, "end": v(147.66, 12.89) * mm});
            skLineSegment(sketch, "E311", {"start": v(147.66, 12.89) * mm, "end": v(147.66, 17.64) * mm});
            skLineSegment(sketch, "E312", {"start": v(147.66, 17.64) * mm, "end": v(133.4, 17.65) * mm});
            skArc(sketch, "E313", {"start": v(133.4, 17.65) * mm, "mid": v(130.5, 17.66) * mm, "end": v(127.58, 17.68) * mm});
            skArc(sketch, "E314", {"start": v(127.58, 17.68) * mm, "mid": v(124.73, 17.72) * mm, "end": v(121.87, 17.78) * mm});
            skArc(sketch, "E315", {"start": v(121.87, 17.78) * mm, "mid": v(119.41, 17.84) * mm, "end": v(116.96, 17.92) * mm});
            skArc(sketch, "E316", {"start": v(116.96, 17.92) * mm, "mid": v(115.55, 17.99) * mm, "end": v(114.16, 18.09) * mm});
            skArc(sketch, "E317", {"start": v(114.16, 18.09) * mm, "mid": v(113.07, 18.16) * mm, "end": v(111.99, 18.2) * mm});
            skArc(sketch, "E318", {"start": v(111.99, 18.2) * mm, "mid": v(110.8, 18.2) * mm, "end": v(109.6, 18.17) * mm});
            skArc(sketch, "E319", {"start": v(109.6, 18.17) * mm, "mid": v(108.47, 18.11) * mm, "end": v(107.35, 18.02) * mm});
            skArc(sketch, "E320", {"start": v(107.35, 18.02) * mm, "mid": v(106.5, 17.92) * mm, "end": v(105.66, 17.76) * mm});
            skLineSegment(sketch, "E321", {"start": v(18.43, 12.9) * mm, "end": v(10.71, 12.56) * mm});
            skLineSegment(sketch, "E322", {"start": v(10.71, 12.56) * mm, "end": v(9.64, 8.6) * mm});
            skArc(sketch, "E323", {"start": v(9.64, 8.6) * mm, "mid": v(9.29, 7.37) * mm, "end": v(8.87, 6.16) * mm});
            skArc(sketch, "E324", {"start": v(8.87, 6.16) * mm, "mid": v(8.58, 5.61) * mm, "end": v(8.13, 5.18) * mm});
            skArc(sketch, "E325", {"start": v(8.13, 5.18) * mm, "mid": v(7.56, 4.87) * mm, "end": v(6.93, 4.74) * mm});
            skArc(sketch, "E326", {"start": v(6.93, 4.74) * mm, "mid": v(5.56, 4.66) * mm, "end": v(4.18, 4.64) * mm});
            skArc(sketch, "E327", {"start": v(4.18, 4.64) * mm, "mid": v(3.1, 4.62) * mm, "end": v(2, 4.56) * mm});
            skArc(sketch, "E328", {"start": v(2, 4.56) * mm, "mid": v(1.31, 4.46) * mm, "end": v(0.63, 4.26) * mm});
            skArc(sketch, "E329", {"start": v(0.63, 4.26) * mm, "mid": v(0.18, 4.04) * mm, "end": v(-0.21, 3.72) * mm});
            skArc(sketch, "E330", {"start": v(-0.21, 3.72) * mm, "mid": v(-0.5, 3.34) * mm, "end": v(-0.7, 2.89) * mm});
            skArc(sketch, "E331", {"start": v(-0.7, 2.89) * mm, "mid": v(-0.81, 2.47) * mm, "end": v(-0.93, 2.06) * mm});
            skArc(sketch, "E332", {"start": v(-0.93, 2.06) * mm, "mid": v(-1.08, 1.53) * mm, "end": v(-1.23, 1) * mm});
            skArc(sketch, "E333", {"start": v(-1.23, 1) * mm, "mid": v(-1.4, 0.44) * mm, "end": v(-1.55, -0.12) * mm});
            skArc(sketch, "E334", {"start": v(-1.55, -0.12) * mm, "mid": v(-1.7, -0.62) * mm, "end": v(-1.83, -1.11) * mm});
            skArc(sketch, "E335", {"start": v(-1.83, -1.11) * mm, "mid": v(-1.98, -1.74) * mm, "end": v(-2.06, -2.39) * mm});
            skArc(sketch, "E336", {"start": v(-2.06, -2.39) * mm, "mid": v(-2, -2.74) * mm, "end": v(-1.77, -3) * mm});
            skArc(sketch, "E337", {"start": v(-1.77, -3) * mm, "mid": v(-1.35, -3.22) * mm, "end": v(-0.9, -3.3) * mm});
            skArc(sketch, "E338", {"start": v(-0.9, -3.3) * mm, "mid": v(0.26, -3.35) * mm, "end": v(1.42, -3.36) * mm});
            skArc(sketch, "E339", {"start": v(1.42, -3.36) * mm, "mid": v(2.19, -3.37) * mm, "end": v(2.95, -3.4) * mm});
            skArc(sketch, "E340", {"start": v(2.95, -3.4) * mm, "mid": v(3.64, -3.45) * mm, "end": v(4.33, -3.52) * mm});
            skArc(sketch, "E341", {"start": v(4.33, -3.52) * mm, "mid": v(4.9, -3.6) * mm, "end": v(5.45, -3.68) * mm});
            skArc(sketch, "E342", {"start": v(5.45, -3.68) * mm, "mid": v(5.67, -3.75) * mm, "end": v(5.85, -3.89) * mm});
            skArc(sketch, "E343", {"start": v(5.85, -3.89) * mm, "mid": v(5.98, -4.1) * mm, "end": v(6, -4.36) * mm});
            skArc(sketch, "E344", {"start": v(6, -4.36) * mm, "mid": v(5.66, -6.14) * mm, "end": v(5.32, -7.91) * mm});
            skArc(sketch, "E345", {"start": v(5.32, -7.91) * mm, "mid": v(4.9, -9.98) * mm, "end": v(4.45, -12.04) * mm});
            skArc(sketch, "E346", {"start": v(4.45, -12.04) * mm, "mid": v(3.89, -14.45) * mm, "end": v(3.3, -16.85) * mm});
            skArc(sketch, "E347", {"start": v(3.3, -16.85) * mm, "mid": v(1.93, -23.06) * mm, "end": v(0.83, -29.34) * mm});
            skArc(sketch, "E348", {"start": v(0.83, -29.34) * mm, "mid": v(1.03, -32.03) * mm, "end": v(2.35, -34.39) * mm});
            skArc(sketch, "E349", {"start": v(2.35, -34.39) * mm, "mid": v(4.63, -36.1) * mm, "end": v(7.38, -36.84) * mm});
            skArc(sketch, "E350", {"start": v(7.38, -36.84) * mm, "mid": v(14.59, -37.21) * mm, "end": v(21.8, -37.35) * mm});
            skLineSegment(sketch, "E351", {"start": v(21.8, -37.35) * mm, "end": v(36.44, -37.36) * mm});
            skLineSegment(sketch, "E352", {"start": v(36.44, -37.36) * mm, "end": v(38.05, -33.34) * mm});
            skArc(sketch, "E353", {"start": v(38.05, -33.34) * mm, "mid": v(38.36, -32.56) * mm, "end": v(38.66, -31.78) * mm});
            skArc(sketch, "E354", {"start": v(38.66, -31.78) * mm, "mid": v(38.93, -31.1) * mm, "end": v(39.18, -30.41) * mm});
            skArc(sketch, "E355", {"start": v(39.18, -30.41) * mm, "mid": v(39.4, -29.82) * mm, "end": v(39.62, -29.24) * mm});
            skArc(sketch, "E356", {"start": v(39.62, -29.24) * mm, "mid": v(39.65, -29.13) * mm, "end": v(39.66, -29.02) * mm});
            skArc(sketch, "E357", {"start": v(39.66, -29.02) * mm, "mid": v(39.62, -28.94) * mm, "end": v(39.54, -28.9) * mm});
            skArc(sketch, "E358", {"start": v(39.54, -28.9) * mm, "mid": v(38.35, -28.92) * mm, "end": v(37.16, -28.94) * mm});
            skArc(sketch, "E359", {"start": v(37.16, -28.94) * mm, "mid": v(35.8, -28.97) * mm, "end": v(34.43, -29.02) * mm});
            skArc(sketch, "E360", {"start": v(34.43, -29.02) * mm, "mid": v(32.8, -29.08) * mm, "end": v(31.17, -29.16) * mm});
            skArc(sketch, "E361", {"start": v(31.17, -29.16) * mm, "mid": v(28.8, -29.27) * mm, "end": v(26.44, -29.35) * mm});
            skArc(sketch, "E362", {"start": v(26.44, -29.35) * mm, "mid": v(25.26, -29.34) * mm, "end": v(24.1, -29.23) * mm});
            skArc(sketch, "E363", {"start": v(24.1, -29.23) * mm, "mid": v(23.41, -29.07) * mm, "end": v(22.78, -28.79) * mm});
            skArc(sketch, "E364", {"start": v(22.78, -28.79) * mm, "mid": v(22.34, -28.43) * mm, "end": v(22.05, -27.94) * mm});
            skArc(sketch, "E365", {"start": v(22.05, -27.94) * mm, "mid": v(21.9, -27.37) * mm, "end": v(21.92, -26.8) * mm});
            skArc(sketch, "E366", {"start": v(21.92, -26.8) * mm, "mid": v(22.16, -25.13) * mm, "end": v(22.44, -23.46) * mm});
            skArc(sketch, "E367", {"start": v(22.44, -23.46) * mm, "mid": v(22.8, -21.46) * mm, "end": v(23.23, -19.47) * mm});
            skArc(sketch, "E368", {"start": v(23.23, -19.47) * mm, "mid": v(23.73, -17.26) * mm, "end": v(24.28, -15.06) * mm});
            skLineSegment(sketch, "E369", {"start": v(24.28, -15.06) * mm, "end": v(27.16, -3.86) * mm});
            skLineSegment(sketch, "E370", {"start": v(27.16, -3.86) * mm, "end": v(35.61, -3.36) * mm});
            skArc(sketch, "E371", {"start": v(35.61, -3.36) * mm, "mid": v(38.23, -3.2) * mm, "end": v(40.84, -3) * mm});
            skArc(sketch, "E372", {"start": v(40.84, -3) * mm, "mid": v(41.9, -2.84) * mm, "end": v(42.94, -2.57) * mm});
            skArc(sketch, "E373", {"start": v(42.94, -2.57) * mm, "mid": v(43.56, -2.26) * mm, "end": v(44.05, -1.78) * mm});
            skArc(sketch, "E374", {"start": v(44.05, -1.78) * mm, "mid": v(44.48, -1.1) * mm, "end": v(44.77, -0.36) * mm});
            skArc(sketch, "E375", {"start": v(44.77, -0.36) * mm, "mid": v(45.14, 1.2) * mm, "end": v(45.42, 2.77) * mm});
            skArc(sketch, "E376", {"start": v(45.42, 2.77) * mm, "mid": v(45.33, 3.47) * mm, "end": v(44.88, 4) * mm});
            skArc(sketch, "E377", {"start": v(44.88, 4) * mm, "mid": v(44.1, 4.4) * mm, "end": v(43.22, 4.55) * mm});
            skArc(sketch, "E378", {"start": v(43.22, 4.55) * mm, "mid": v(40.38, 4.62) * mm, "end": v(37.55, 4.64) * mm});
            skLineSegment(sketch, "E379", {"start": v(37.55, 4.64) * mm, "end": v(29.44, 4.64) * mm});
            skLineSegment(sketch, "E380", {"start": v(29.44, 4.64) * mm, "end": v(30.1, 7.39) * mm});
            skArc(sketch, "E381", {"start": v(30.1, 7.39) * mm, "mid": v(30.24, 7.98) * mm, "end": v(30.38, 8.57) * mm});
            skArc(sketch, "E382", {"start": v(30.38, 8.57) * mm, "mid": v(30.55, 9.2) * mm, "end": v(30.71, 9.85) * mm});
            skArc(sketch, "E383", {"start": v(30.71, 9.85) * mm, "mid": v(30.87, 10.44) * mm, "end": v(31.03, 11.03) * mm});
            skArc(sketch, "E384", {"start": v(31.03, 11.03) * mm, "mid": v(31.15, 11.46) * mm, "end": v(31.27, 11.89) * mm});
            skArc(sketch, "E385", {"start": v(31.27, 11.89) * mm, "mid": v(31.36, 12.32) * mm, "end": v(31.4, 12.76) * mm});
            skArc(sketch, "E386", {"start": v(31.4, 12.76) * mm, "mid": v(31.32, 13.04) * mm, "end": v(31.13, 13.25) * mm});
            skArc(sketch, "E387", {"start": v(31.13, 13.25) * mm, "mid": v(30.8, 13.41) * mm, "end": v(30.42, 13.47) * mm});
            skArc(sketch, "E388", {"start": v(30.42, 13.47) * mm, "mid": v(29.7, 13.47) * mm, "end": v(28.97, 13.44) * mm});
            skArc(sketch, "E389", {"start": v(28.97, 13.44) * mm, "mid": v(28.2, 13.39) * mm, "end": v(27.41, 13.34) * mm});
            skArc(sketch, "E390", {"start": v(27.41, 13.34) * mm, "mid": v(26.06, 13.27) * mm, "end": v(24.72, 13.2) * mm});
            skArc(sketch, "E391", {"start": v(24.72, 13.2) * mm, "mid": v(23.16, 13.12) * mm, "end": v(21.6, 13.04) * mm});
            skArc(sketch, "E392", {"start": v(21.6, 13.04) * mm, "mid": v(20.02, 12.97) * mm, "end": v(18.43, 12.9) * mm});
            skArc(sketch, "E393", {"start": v(-92.97, 2.29) * mm, "mid": v(-92.86, 1.54) * mm, "end": v(-92.88, 0.78) * mm});
            skArc(sketch, "E394", {"start": v(-92.88, 0.78) * mm, "mid": v(-93.14, -1.1) * mm, "end": v(-93.43, -2.96) * mm});
            skArc(sketch, "E395", {"start": v(-93.43, -2.96) * mm, "mid": v(-93.82, -5.2) * mm, "end": v(-94.26, -7.42) * mm});
            skArc(sketch, "E396", {"start": v(-94.26, -7.42) * mm, "mid": v(-94.8, -9.85) * mm, "end": v(-95.36, -12.27) * mm});
            skArc(sketch, "E397", {"start": v(-95.36, -12.27) * mm, "mid": v(-97, -19.6) * mm, "end": v(-98.33, -26.98) * mm});
            skArc(sketch, "E398", {"start": v(-98.33, -26.98) * mm, "mid": v(-98.27, -30.28) * mm, "end": v(-97.06, -33.35) * mm});
            skArc(sketch, "E399", {"start": v(-97.06, -33.35) * mm, "mid": v(-94.95, -35.5) * mm, "end": v(-92.13, -36.55) * mm});
            skArc(sketch, "E400", {"start": v(-92.13, -36.55) * mm, "mid": v(-86.03, -37.16) * mm, "end": v(-79.91, -37.36) * mm});
            skArc(sketch, "E401", {"start": v(-79.91, -37.36) * mm, "mid": v(-77.02, -37.34) * mm, "end": v(-74.12, -37.29) * mm});
            skArc(sketch, "E402", {"start": v(-74.12, -37.29) * mm, "mid": v(-72.53, -37.2) * mm, "end": v(-70.96, -37) * mm});
            skArc(sketch, "E403", {"start": v(-70.96, -37) * mm, "mid": v(-69.88, -36.75) * mm, "end": v(-68.83, -36.38) * mm});
            skArc(sketch, "E404", {"start": v(-68.83, -36.38) * mm, "mid": v(-67.87, -35.9) * mm, "end": v(-66.98, -35.29) * mm});
            skLineSegment(sketch, "E405", {"start": v(-66.98, -35.29) * mm, "end": v(-64.34, -33.22) * mm});
            skLineSegment(sketch, "E406", {"start": v(-64.34, -33.22) * mm, "end": v(-64.34, -35.29) * mm});
            skArc(sketch, "E407", {"start": v(-64.34, -35.29) * mm, "mid": v(-64.23, -35.9) * mm, "end": v(-63.91, -36.43) * mm});
            skArc(sketch, "E408", {"start": v(-63.91, -36.43) * mm, "mid": v(-63.42, -36.84) * mm, "end": v(-62.81, -37.06) * mm});
            skArc(sketch, "E409", {"start": v(-62.81, -37.06) * mm, "mid": v(-61.6, -37.24) * mm, "end": v(-60.37, -37.31) * mm});
            skArc(sketch, "E410", {"start": v(-60.37, -37.31) * mm, "mid": v(-57.05, -37.35) * mm, "end": v(-53.74, -37.36) * mm});
            skLineSegment(sketch, "E411", {"start": v(-53.74, -37.36) * mm, "end": v(-43.13, -37.36) * mm});
            skLineSegment(sketch, "E412", {"start": v(-43.13, -37.36) * mm, "end": v(-43.73, -34.98) * mm});
            skArc(sketch, "E413", {"start": v(-43.73, -34.98) * mm, "mid": v(-43.85, -34.13) * mm, "end": v(-43.8, -33.28) * mm});
            skArc(sketch, "E414", {"start": v(-43.8, -33.28) * mm, "mid": v(-43.35, -30.7) * mm, "end": v(-42.88, -28.12) * mm});
            skArc(sketch, "E415", {"start": v(-42.88, -28.12) * mm, "mid": v(-42.25, -24.95) * mm, "end": v(-41.57, -21.8) * mm});
            skArc(sketch, "E416", {"start": v(-41.57, -21.8) * mm, "mid": v(-40.72, -18.1) * mm, "end": v(-39.83, -14.43) * mm});
            skArc(sketch, "E417", {"start": v(-39.83, -14.43) * mm, "mid": v(-38.97, -10.93) * mm, "end": v(-38.11, -7.43) * mm});
            skArc(sketch, "E418", {"start": v(-38.11, -7.43) * mm, "mid": v(-37.39, -4.45) * mm, "end": v(-36.66, -1.47) * mm});
            skArc(sketch, "E419", {"start": v(-36.66, -1.47) * mm, "mid": v(-36.02, 1.18) * mm, "end": v(-35.39, 3.83) * mm});
            skArc(sketch, "E420", {"start": v(-35.39, 3.83) * mm, "mid": v(-35.35, 4.01) * mm, "end": v(-35.34, 4.19) * mm});
            skArc(sketch, "E421", {"start": v(-35.34, 4.19) * mm, "mid": v(-35.4, 4.32) * mm, "end": v(-35.52, 4.37) * mm});
            skArc(sketch, "E422", {"start": v(-35.52, 4.37) * mm, "mid": v(-37.05, 4.44) * mm, "end": v(-38.58, 4.5) * mm});
            skArc(sketch, "E423", {"start": v(-38.58, 4.5) * mm, "mid": v(-40.35, 4.57) * mm, "end": v(-42.13, 4.6) * mm});
            skArc(sketch, "E424", {"start": v(-42.13, 4.6) * mm, "mid": v(-44.23, 4.63) * mm, "end": v(-46.34, 4.64) * mm});
            skLineSegment(sketch, "E425", {"start": v(-46.34, 4.64) * mm, "end": v(-57.34, 4.64) * mm});
            skLineSegment(sketch, "E426", {"start": v(-57.34, 4.64) * mm, "end": v(-57.34, 1.08) * mm});
            skArc(sketch, "E427", {"start": v(-57.34, 1.08) * mm, "mid": v(-57.47, -1.31) * mm, "end": v(-57.86, -3.67) * mm});
            skArc(sketch, "E428", {"start": v(-57.86, -3.67) * mm, "mid": v(-59.1, -9.06) * mm, "end": v(-60.38, -14.43) * mm});
            skArc(sketch, "E429", {"start": v(-60.38, -14.43) * mm, "mid": v(-61.77, -19.97) * mm, "end": v(-63.2, -25.5) * mm});
            skArc(sketch, "E430", {"start": v(-63.2, -25.5) * mm, "mid": v(-63.73, -26.87) * mm, "end": v(-64.54, -28.1) * mm});
            skArc(sketch, "E431", {"start": v(-64.54, -28.1) * mm, "mid": v(-65.33, -28.74) * mm, "end": v(-66.3, -29.03) * mm});
            skArc(sketch, "E432", {"start": v(-66.3, -29.03) * mm, "mid": v(-68.8, -29.24) * mm, "end": v(-71.3, -29.35) * mm});
            skArc(sketch, "E433", {"start": v(-71.3, -29.35) * mm, "mid": v(-73.8, -29.37) * mm, "end": v(-76.32, -29.3) * mm});
            skArc(sketch, "E434", {"start": v(-76.32, -29.3) * mm, "mid": v(-77.16, -29.06) * mm, "end": v(-77.8, -28.44) * mm});
            skArc(sketch, "E435", {"start": v(-77.8, -28.44) * mm, "mid": v(-77.94, -28.08) * mm, "end": v(-77.94, -27.7) * mm});
            skArc(sketch, "E436", {"start": v(-77.94, -27.7) * mm, "mid": v(-77.56, -25.59) * mm, "end": v(-77.17, -23.47) * mm});
            skArc(sketch, "E437", {"start": v(-77.17, -23.47) * mm, "mid": v(-76.68, -21) * mm, "end": v(-76.16, -18.53) * mm});
            skArc(sketch, "E438", {"start": v(-76.16, -18.53) * mm, "mid": v(-75.52, -15.68) * mm, "end": v(-74.86, -12.84) * mm});
            skArc(sketch, "E439", {"start": v(-74.86, -12.84) * mm, "mid": v(-74.18, -9.98) * mm, "end": v(-73.5, -7.11) * mm});
            skArc(sketch, "E440", {"start": v(-73.5, -7.11) * mm, "mid": v(-72.94, -4.59) * mm, "end": v(-72.38, -2.06) * mm});
            skArc(sketch, "E441", {"start": v(-72.38, -2.06) * mm, "mid": v(-71.9, 0.09) * mm, "end": v(-71.45, 2.24) * mm});
            skArc(sketch, "E442", {"start": v(-71.45, 2.24) * mm, "mid": v(-71.37, 2.74) * mm, "end": v(-71.34, 3.24) * mm});
            skArc(sketch, "E443", {"start": v(-71.34, 3.24) * mm, "mid": v(-71.48, 3.68) * mm, "end": v(-71.85, 3.95) * mm});
            skArc(sketch, "E444", {"start": v(-71.85, 3.95) * mm, "mid": v(-72.7, 4.2) * mm, "end": v(-73.58, 4.36) * mm});
            skArc(sketch, "E445", {"start": v(-73.58, 4.36) * mm, "mid": v(-75.13, 4.51) * mm, "end": v(-76.69, 4.58) * mm});
            skArc(sketch, "E446", {"start": v(-76.69, 4.58) * mm, "mid": v(-79.57, 4.63) * mm, "end": v(-82.45, 4.64) * mm});
            skLineSegment(sketch, "E447", {"start": v(-82.45, 4.64) * mm, "end": v(-93.56, 4.64) * mm});
            skLineSegment(sketch, "E448", {"start": v(-93.56, 4.64) * mm, "end": v(-92.97, 2.29) * mm});
            skArc(sketch, "E449", {"start": v(52.63, 0.89) * mm, "mid": v(52.44, -2.2) * mm, "end": v(51.9, -5.26) * mm});
            skArc(sketch, "E450", {"start": v(51.9, -5.26) * mm, "mid": v(50.3, -11.9) * mm, "end": v(48.6, -18.53) * mm});
            skArc(sketch, "E451", {"start": v(48.6, -18.53) * mm, "mid": v(46.79, -25.35) * mm, "end": v(44.9, -32.16) * mm});
            skArc(sketch, "E452", {"start": v(44.9, -32.16) * mm, "mid": v(44.19, -33.9) * mm, "end": v(43.1, -35.43) * mm});
            skArc(sketch, "E453", {"start": v(43.1, -35.43) * mm, "mid": v(42.8, -35.9) * mm, "end": v(42.7, -36.47) * mm});
            skArc(sketch, "E454", {"start": v(42.7, -36.47) * mm, "mid": v(42.85, -36.88) * mm, "end": v(43.23, -37.1) * mm});
            skArc(sketch, "E455", {"start": v(43.23, -37.1) * mm, "mid": v(44.44, -37.27) * mm, "end": v(45.65, -37.33) * mm});
            skArc(sketch, "E456", {"start": v(45.65, -37.33) * mm, "mid": v(49.83, -37.35) * mm, "end": v(54, -37.36) * mm});
            skLineSegment(sketch, "E457", {"start": v(54, -37.36) * mm, "end": v(66.66, -37.36) * mm});
            skLineSegment(sketch, "E458", {"start": v(66.66, -37.36) * mm, "end": v(66.66, -33.81) * mm});
            skArc(sketch, "E459", {"start": v(66.66, -33.81) * mm, "mid": v(66.7, -32.7) * mm, "end": v(66.85, -31.6) * mm});
            skArc(sketch, "E460", {"start": v(66.85, -31.6) * mm, "mid": v(67.33, -29.03) * mm, "end": v(67.83, -26.45) * mm});
            skArc(sketch, "E461", {"start": v(67.83, -26.45) * mm, "mid": v(68.46, -23.39) * mm, "end": v(69.12, -20.33) * mm});
            skArc(sketch, "E462", {"start": v(69.12, -20.33) * mm, "mid": v(69.88, -17.03) * mm, "end": v(70.66, -13.74) * mm});
            skArc(sketch, "E463", {"start": v(70.66, -13.74) * mm, "mid": v(71.43, -10.54) * mm, "end": v(72.19, -7.34) * mm});
            skArc(sketch, "E464", {"start": v(72.19, -7.34) * mm, "mid": v(72.84, -4.57) * mm, "end": v(73.48, -1.8) * mm});
            skArc(sketch, "E465", {"start": v(73.48, -1.8) * mm, "mid": v(74.03, 0.61) * mm, "end": v(74.58, 3.02) * mm});
            skArc(sketch, "E466", {"start": v(74.58, 3.02) * mm, "mid": v(74.64, 3.36) * mm, "end": v(74.66, 3.71) * mm});
            skArc(sketch, "E467", {"start": v(74.66, 3.71) * mm, "mid": v(74.56, 3.96) * mm, "end": v(74.32, 4.09) * mm});
            skArc(sketch, "E468", {"start": v(74.32, 4.09) * mm, "mid": v(72.88, 4.24) * mm, "end": v(71.43, 4.37) * mm});
            skArc(sketch, "E469", {"start": v(71.43, 4.37) * mm, "mid": v(69.66, 4.5) * mm, "end": v(67.89, 4.57) * mm});
            skArc(sketch, "E470", {"start": v(67.89, 4.57) * mm, "mid": v(65.77, 4.62) * mm, "end": v(63.66, 4.64) * mm});
            skLineSegment(sketch, "E471", {"start": v(63.66, 4.64) * mm, "end": v(52.66, 4.64) * mm});
            skLineSegment(sketch, "E472", {"start": v(52.66, 4.64) * mm, "end": v(52.63, 0.89) * mm});
            skArc(sketch, "E473", {"start": v(157.06, 0.74) * mm, "mid": v(155.68, -0.3) * mm, "end": v(154.52, -1.57) * mm});
            skArc(sketch, "E474", {"start": v(154.52, -1.57) * mm, "mid": v(153.42, -3.23) * mm, "end": v(152.54, -5.03) * mm});
            skArc(sketch, "E475", {"start": v(152.54, -5.03) * mm, "mid": v(151.5, -7.79) * mm, "end": v(150.64, -10.62) * mm});
            skArc(sketch, "E476", {"start": v(150.64, -10.62) * mm, "mid": v(149.36, -15.59) * mm, "end": v(148.14, -20.58) * mm});
            skArc(sketch, "E477", {"start": v(148.14, -20.58) * mm, "mid": v(147.31, -24.18) * mm, "end": v(146.5, -27.79) * mm});
            skArc(sketch, "E478", {"start": v(146.5, -27.79) * mm, "mid": v(146.22, -29.35) * mm, "end": v(146.04, -30.94) * mm});
            skArc(sketch, "E479", {"start": v(146.04, -30.94) * mm, "mid": v(146.04, -31.95) * mm, "end": v(146.2, -32.95) * mm});
            skArc(sketch, "E480", {"start": v(146.2, -32.95) * mm, "mid": v(146.53, -33.9) * mm, "end": v(147.01, -34.78) * mm});
            skArc(sketch, "E481", {"start": v(147.01, -34.78) * mm, "mid": v(148.07, -35.98) * mm, "end": v(149.43, -36.83) * mm});
            skArc(sketch, "E482", {"start": v(149.43, -36.83) * mm, "mid": v(151.33, -37.5) * mm, "end": v(153.3, -37.87) * mm});
            skArc(sketch, "E483", {"start": v(153.3, -37.87) * mm, "mid": v(156.78, -38.17) * mm, "end": v(160.27, -38.27) * mm});
            skArc(sketch, "E484", {"start": v(160.27, -38.27) * mm, "mid": v(168.16, -38.24) * mm, "end": v(176.06, -38.15) * mm});
            skLineSegment(sketch, "E485", {"start": v(176.06, -38.15) * mm, "end": v(196.97, -37.86) * mm});
            skLineSegment(sketch, "E486", {"start": v(196.97, -37.86) * mm, "end": v(198.66, -33.86) * mm});
            skLineSegment(sketch, "E487", {"start": v(198.66, -33.86) * mm, "end": v(200.36, -29.86) * mm});
            skLineSegment(sketch, "E488", {"start": v(200.36, -29.86) * mm, "end": v(184.7, -30.2) * mm});
            skArc(sketch, "E489", {"start": v(184.7, -30.2) * mm, "mid": v(178.98, -30.28) * mm, "end": v(173.25, -30.3) * mm});
            skArc(sketch, "E490", {"start": v(173.25, -30.3) * mm, "mid": v(171.12, -30.14) * mm, "end": v(169.04, -29.66) * mm});
            skArc(sketch, "E491", {"start": v(169.04, -29.66) * mm, "mid": v(168.02, -29.01) * mm, "end": v(167.46, -27.94) * mm});
            skArc(sketch, "E492", {"start": v(167.46, -27.94) * mm, "mid": v(167.3, -26.37) * mm, "end": v(167.51, -24.8) * mm});
            skLineSegment(sketch, "E493", {"start": v(167.51, -24.8) * mm, "end": v(168.3, -21.86) * mm});
            skLineSegment(sketch, "E494", {"start": v(168.3, -21.86) * mm, "end": v(185.8, -21.59) * mm});
            skLineSegment(sketch, "E495", {"start": v(185.8, -21.59) * mm, "end": v(203.3, -21.32) * mm});
            skLineSegment(sketch, "E496", {"start": v(203.3, -21.32) * mm, "end": v(205, -14.09) * mm});
            skArc(sketch, "E497", {"start": v(205, -14.09) * mm, "mid": v(206.05, -8.85) * mm, "end": v(206.78, -3.56) * mm});
            skArc(sketch, "E498", {"start": v(206.78, -3.56) * mm, "mid": v(206.42, -1.26) * mm, "end": v(204.93, 0.54) * mm});
            skArc(sketch, "E499", {"start": v(204.93, 0.54) * mm, "mid": v(202.34, 1.84) * mm, "end": v(199.5, 2.35) * mm});
            skArc(sketch, "E500", {"start": v(199.5, 2.35) * mm, "mid": v(190.34, 2.57) * mm, "end": v(181.18, 2.64) * mm});
            skArc(sketch, "E501", {"start": v(181.18, 2.64) * mm, "mid": v(175.04, 2.62) * mm, "end": v(168.9, 2.58) * mm});
            skArc(sketch, "E502", {"start": v(168.9, 2.58) * mm, "mid": v(165.99, 2.5) * mm, "end": v(163.1, 2.32) * mm});
            skArc(sketch, "E503", {"start": v(163.1, 2.32) * mm, "mid": v(161.33, 2.12) * mm, "end": v(159.6, 1.78) * mm});
            skArc(sketch, "E504", {"start": v(159.6, 1.78) * mm, "mid": v(158.28, 1.36) * mm, "end": v(157.06, 0.74) * mm});
            skArc(sketch, "E505", {"start": v(186.3, -5.87) * mm, "mid": v(186.42, -6.27) * mm, "end": v(186.48, -6.68) * mm});
            skArc(sketch, "E506", {"start": v(186.48, -6.68) * mm, "mid": v(186.5, -7.32) * mm, "end": v(186.51, -7.96) * mm});
            skArc(sketch, "E507", {"start": v(186.51, -7.96) * mm, "mid": v(186.49, -8.7) * mm, "end": v(186.43, -9.42) * mm});
            skArc(sketch, "E508", {"start": v(186.43, -9.42) * mm, "mid": v(186.34, -10.15) * mm, "end": v(186.22, -10.87) * mm});
            skLineSegment(sketch, "E509", {"start": v(186.22, -10.87) * mm, "end": v(185.57, -14.36) * mm});
            skLineSegment(sketch, "E510", {"start": v(185.57, -14.36) * mm, "end": v(178, -14.36) * mm});
            skLineSegment(sketch, "E511", {"start": v(178, -14.36) * mm, "end": v(170.43, -14.36) * mm});
            skLineSegment(sketch, "E512", {"start": v(170.43, -14.36) * mm, "end": v(171.1, -10.61) * mm});
            skArc(sketch, "E513", {"start": v(171.1, -10.61) * mm, "mid": v(171.27, -9.84) * mm, "end": v(171.49, -9.08) * mm});
            skArc(sketch, "E514", {"start": v(171.49, -9.08) * mm, "mid": v(171.75, -8.33) * mm, "end": v(172.06, -7.6) * mm});
            skArc(sketch, "E515", {"start": v(172.06, -7.6) * mm, "mid": v(172.38, -6.96) * mm, "end": v(172.74, -6.35) * mm});
            skArc(sketch, "E516", {"start": v(172.74, -6.35) * mm, "mid": v(173.04, -5.95) * mm, "end": v(173.41, -5.61) * mm});
            skArc(sketch, "E517", {"start": v(173.41, -5.61) * mm, "mid": v(174.62, -4.91) * mm, "end": v(175.98, -4.56) * mm});
            skArc(sketch, "E518", {"start": v(175.98, -4.56) * mm, "mid": v(178.22, -4.37) * mm, "end": v(180.48, -4.34) * mm});
            skArc(sketch, "E519", {"start": v(180.48, -4.34) * mm, "mid": v(182.66, -4.45) * mm, "end": v(184.84, -4.7) * mm});
            skArc(sketch, "E520", {"start": v(184.84, -4.7) * mm, "mid": v(185.72, -5.08) * mm, "end": v(186.3, -5.87) * mm});
            skArc(sketch, "E521", {"start": v(215.66, -0.91) * mm, "mid": v(215.5, -3.54) * mm, "end": v(215.07, -6.13) * mm});
            skArc(sketch, "E522", {"start": v(215.07, -6.13) * mm, "mid": v(213.6, -12.39) * mm, "end": v(212.08, -18.63) * mm});
            skArc(sketch, "E523", {"start": v(212.08, -18.63) * mm, "mid": v(210.46, -24.95) * mm, "end": v(208.8, -31.25) * mm});
            skArc(sketch, "E524", {"start": v(208.8, -31.25) * mm, "mid": v(208.1, -33.23) * mm, "end": v(207.1, -35.08) * mm});
            skArc(sketch, "E525", {"start": v(207.1, -35.08) * mm, "mid": v(206.81, -35.52) * mm, "end": v(206.54, -35.96) * mm});
            skArc(sketch, "E526", {"start": v(206.54, -35.96) * mm, "mid": v(206.3, -36.38) * mm, "end": v(206.08, -36.8) * mm});
            skArc(sketch, "E527", {"start": v(206.08, -36.8) * mm, "mid": v(205.9, -37.15) * mm, "end": v(205.73, -37.5) * mm});
            skArc(sketch, "E528", {"start": v(205.73, -37.5) * mm, "mid": v(205.67, -37.66) * mm, "end": v(205.66, -37.83) * mm});
            skArc(sketch, "E529", {"start": v(205.66, -37.83) * mm, "mid": v(205.72, -37.97) * mm, "end": v(205.86, -38.04) * mm});
            skArc(sketch, "E530", {"start": v(205.86, -38.04) * mm, "mid": v(207.52, -38.13) * mm, "end": v(209.19, -38.2) * mm});
            skArc(sketch, "E531", {"start": v(209.19, -38.2) * mm, "mid": v(211.13, -38.28) * mm, "end": v(213.07, -38.32) * mm});
            skArc(sketch, "E532", {"start": v(213.07, -38.32) * mm, "mid": v(215.37, -38.35) * mm, "end": v(217.68, -38.36) * mm});
            skLineSegment(sketch, "E533", {"start": v(217.68, -38.36) * mm, "end": v(229.7, -38.36) * mm});
            skLineSegment(sketch, "E534", {"start": v(229.7, -38.36) * mm, "end": v(229.11, -36.05) * mm});
            skArc(sketch, "E535", {"start": v(229.11, -36.05) * mm, "mid": v(228.87, -34.2) * mm, "end": v(229.07, -32.34) * mm});
            skArc(sketch, "E536", {"start": v(229.07, -32.34) * mm, "mid": v(230.52, -26.14) * mm, "end": v(232.03, -19.95) * mm});
            skArc(sketch, "E537", {"start": v(232.03, -19.95) * mm, "mid": v(233.65, -13.62) * mm, "end": v(235.3, -7.3) * mm});
            skArc(sketch, "E538", {"start": v(235.3, -7.3) * mm, "mid": v(235.87, -6.13) * mm, "end": v(236.83, -5.23) * mm});
            skArc(sketch, "E539", {"start": v(236.83, -5.23) * mm, "mid": v(237.87, -4.74) * mm, "end": v(239, -4.52) * mm});
            skArc(sketch, "E540", {"start": v(239, -4.52) * mm, "mid": v(241.16, -4.41) * mm, "end": v(243.32, -4.4) * mm});
            skArc(sketch, "E541", {"start": v(243.32, -4.4) * mm, "mid": v(245.48, -4.48) * mm, "end": v(247.64, -4.64) * mm});
            skArc(sketch, "E542", {"start": v(247.64, -4.64) * mm, "mid": v(248.55, -4.89) * mm, "end": v(249.33, -5.43) * mm});
            skArc(sketch, "E543", {"start": v(249.33, -5.43) * mm, "mid": v(249.89, -6.38) * mm, "end": v(249.92, -7.48) * mm});
            skArc(sketch, "E544", {"start": v(249.92, -7.48) * mm, "mid": v(248.53, -13.61) * mm, "end": v(247.08, -19.74) * mm});
            skArc(sketch, "E545", {"start": v(247.08, -19.74) * mm, "mid": v(245.65, -25.53) * mm, "end": v(244.1, -31.3) * mm});
            skArc(sketch, "E546", {"start": v(244.1, -31.3) * mm, "mid": v(243.24, -33.7) * mm, "end": v(242, -35.95) * mm});
            skLineSegment(sketch, "E547", {"start": v(242, -35.95) * mm, "end": v(240.43, -38.36) * mm});
            skLineSegment(sketch, "E548", {"start": v(240.43, -38.36) * mm, "end": v(252.54, -38.36) * mm});
            skLineSegment(sketch, "E549", {"start": v(252.54, -38.36) * mm, "end": v(264.66, -38.36) * mm});
            skLineSegment(sketch, "E550", {"start": v(264.66, -38.36) * mm, "end": v(264.66, -34.92) * mm});
            skArc(sketch, "E551", {"start": v(264.66, -34.92) * mm, "mid": v(264.7, -33.9) * mm, "end": v(264.82, -32.9) * mm});
            skArc(sketch, "E552", {"start": v(264.82, -32.9) * mm, "mid": v(265.17, -30.88) * mm, "end": v(265.54, -28.88) * mm});
            skArc(sketch, "E553", {"start": v(265.54, -28.88) * mm, "mid": v(266.01, -26.5) * mm, "end": v(266.52, -24.14) * mm});
            skArc(sketch, "E554", {"start": v(266.52, -24.14) * mm, "mid": v(267.08, -21.65) * mm, "end": v(267.67, -19.17) * mm});
            skArc(sketch, "E555", {"start": v(267.67, -19.17) * mm, "mid": v(268.7, -14.77) * mm, "end": v(269.63, -10.34) * mm});
            skArc(sketch, "E556", {"start": v(269.63, -10.34) * mm, "mid": v(269.97, -7.86) * mm, "end": v(270.02, -5.36) * mm});
            skArc(sketch, "E557", {"start": v(270.02, -5.36) * mm, "mid": v(269.77, -3.65) * mm, "end": v(269.15, -2.04) * mm});
            skArc(sketch, "E558", {"start": v(269.15, -2.04) * mm, "mid": v(268.2, -0.59) * mm, "end": v(266.94, 0.63) * mm});
            skArc(sketch, "E559", {"start": v(266.94, 0.63) * mm, "mid": v(266.04, 1.24) * mm, "end": v(265.06, 1.7) * mm});
            skArc(sketch, "E560", {"start": v(265.05, 1.7) * mm, "mid": v(263.92, 2.07) * mm, "end": v(262.76, 2.3) * mm});
            skArc(sketch, "E561", {"start": v(262.76, 2.3) * mm, "mid": v(260.99, 2.49) * mm, "end": v(259.2, 2.57) * mm});
            skArc(sketch, "E562", {"start": v(259.2, 2.57) * mm, "mid": v(255.77, 2.62) * mm, "end": v(252.34, 2.64) * mm});
            skArc(sketch, "E563", {"start": v(252.34, 2.64) * mm, "mid": v(248.75, 2.62) * mm, "end": v(245.17, 2.58) * mm});
            skArc(sketch, "E564", {"start": v(245.17, 2.58) * mm, "mid": v(243.5, 2.5) * mm, "end": v(241.82, 2.3) * mm});
            skArc(sketch, "E565", {"start": v(241.82, 2.3) * mm, "mid": v(240.75, 2.05) * mm, "end": v(239.73, 1.66) * mm});
            skArc(sketch, "E566", {"start": v(239.73, 1.66) * mm, "mid": v(238.8, 1.13) * mm, "end": v(237.97, 0.47) * mm});
            skLineSegment(sketch, "E567", {"start": v(237.97, 0.47) * mm, "end": v(235.66, -1.7) * mm});
            skLineSegment(sketch, "E568", {"start": v(235.66, -1.7) * mm, "end": v(235.66, 0.47) * mm});
            skArc(sketch, "E569", {"start": v(235.66, 0.47) * mm, "mid": v(235.56, 1.1) * mm, "end": v(235.26, 1.68) * mm});
            skArc(sketch, "E570", {"start": v(235.26, 1.68) * mm, "mid": v(234.82, 2.1) * mm, "end": v(234.26, 2.34) * mm});
            skArc(sketch, "E571", {"start": v(234.26, 2.34) * mm, "mid": v(233.13, 2.52) * mm, "end": v(232, 2.6) * mm});
            skArc(sketch, "E572", {"start": v(232, 2.6) * mm, "mid": v(228.83, 2.63) * mm, "end": v(225.66, 2.64) * mm});
            skLineSegment(sketch, "E573", {"start": v(225.66, 2.64) * mm, "end": v(215.66, 2.64) * mm});
            skLineSegment(sketch, "E574", {"start": v(215.66, 2.64) * mm, "end": v(215.66, -0.91) * mm});
            skArc(sketch, "E575", {"start": v(285.16, 0.8) * mm, "mid": v(284.53, 0.4) * mm, "end": v(283.91, -0.02) * mm});
            skArc(sketch, "E576", {"start": v(283.91, -0.02) * mm, "mid": v(283.27, -0.49) * mm, "end": v(282.65, -0.97) * mm});
            skArc(sketch, "E577", {"start": v(282.65, -0.97) * mm, "mid": v(282.09, -1.43) * mm, "end": v(281.55, -1.9) * mm});
            skArc(sketch, "E578", {"start": v(281.55, -1.9) * mm, "mid": v(281.17, -2.26) * mm, "end": v(280.83, -2.64) * mm});
            skArc(sketch, "E579", {"start": v(280.83, -2.64) * mm, "mid": v(280.05, -3.78) * mm, "end": v(279.5, -5.03) * mm});
            skArc(sketch, "E580", {"start": v(279.5, -5.03) * mm, "mid": v(278.75, -7.33) * mm, "end": v(278.1, -9.66) * mm});
            skArc(sketch, "E581", {"start": v(278.1, -9.66) * mm, "mid": v(277.5, -12.12) * mm, "end": v(277.02, -14.6) * mm});
            skArc(sketch, "E582", {"start": v(277.02, -14.6) * mm, "mid": v(276.76, -16.57) * mm, "end": v(276.67, -18.55) * mm});
            skArc(sketch, "E583", {"start": v(276.67, -18.55) * mm, "mid": v(276.86, -20.38) * mm, "end": v(277.43, -22.12) * mm});
            skArc(sketch, "E584", {"start": v(277.43, -22.12) * mm, "mid": v(278.3, -23.35) * mm, "end": v(279.57, -24.17) * mm});
            skArc(sketch, "E585", {"start": v(279.57, -24.17) * mm, "mid": v(281.73, -24.84) * mm, "end": v(283.97, -25.14) * mm});
            skArc(sketch, "E586", {"start": v(283.97, -25.14) * mm, "mid": v(288.67, -25.3) * mm, "end": v(293.38, -25.36) * mm});
            skArc(sketch, "E587", {"start": v(293.38, -25.36) * mm, "mid": v(297.18, -25.37) * mm, "end": v(300.97, -25.4) * mm});
            skArc(sketch, "E588", {"start": v(300.97, -25.4) * mm, "mid": v(302.41, -25.48) * mm, "end": v(303.84, -25.65) * mm});
            skArc(sketch, "E589", {"start": v(303.84, -25.65) * mm, "mid": v(304.54, -25.86) * mm, "end": v(305.15, -26.25) * mm});
            skArc(sketch, "E590", {"start": v(305.15, -26.25) * mm, "mid": v(305.52, -26.73) * mm, "end": v(305.66, -27.33) * mm});
            skArc(sketch, "E591", {"start": v(305.66, -27.33) * mm, "mid": v(305.41, -28.5) * mm, "end": v(304.71, -29.47) * mm});
            skArc(sketch, "E592", {"start": v(304.71, -29.47) * mm, "mid": v(303.57, -30.27) * mm, "end": v(302.25, -30.75) * mm});
            skArc(sketch, "E593", {"start": v(302.25, -30.75) * mm, "mid": v(299.89, -31.14) * mm, "end": v(297.5, -31.27) * mm});
            skArc(sketch, "E594", {"start": v(297.5, -31.27) * mm, "mid": v(293.11, -31.2) * mm, "end": v(288.74, -31.06) * mm});
            skArc(sketch, "E595", {"start": v(288.74, -31.06) * mm, "mid": v(286.24, -30.94) * mm, "end": v(283.75, -30.8) * mm});
            skArc(sketch, "E596", {"start": v(283.75, -30.8) * mm, "mid": v(281.47, -30.65) * mm, "end": v(279.2, -30.47) * mm});
            skArc(sketch, "E597", {"start": v(279.2, -30.47) * mm, "mid": v(277.28, -30.3) * mm, "end": v(275.38, -30.12) * mm});
            skArc(sketch, "E598", {"start": v(275.38, -30.12) * mm, "mid": v(274.64, -30) * mm, "end": v(273.9, -29.82) * mm});
            skArc(sketch, "E599", {"start": v(273.9, -29.82) * mm, "mid": v(273.27, -29.66) * mm, "end": v(272.61, -29.58) * mm});
            skArc(sketch, "E600", {"start": v(272.61, -29.58) * mm, "mid": v(272.25, -29.66) * mm, "end": v(272, -29.92) * mm});
            skArc(sketch, "E601", {"start": v(272, -29.92) * mm, "mid": v(271.79, -30.4) * mm, "end": v(271.7, -30.9) * mm});
            skArc(sketch, "E602", {"start": v(271.7, -30.9) * mm, "mid": v(271.67, -32.33) * mm, "end": v(271.66, -33.74) * mm});
            skLineSegment(sketch, "E603", {"start": v(271.66, -33.74) * mm, "end": v(271.66, -38.36) * mm});
            skLineSegment(sketch, "E604", {"start": v(271.66, -38.36) * mm, "end": v(292.4, -38.34) * mm});
            skArc(sketch, "E605", {"start": v(292.4, -38.34) * mm, "mid": v(301.6, -38.23) * mm, "end": v(310.77, -37.93) * mm});
            skArc(sketch, "E606", {"start": v(310.77, -37.93) * mm, "mid": v(314.68, -37.37) * mm, "end": v(318.4, -36.05) * mm});
            skArc(sketch, "E607", {"start": v(318.4, -36.05) * mm, "mid": v(320.96, -34.24) * mm, "end": v(322.77, -31.68) * mm});
            skArc(sketch, "E608", {"start": v(322.77, -31.68) * mm, "mid": v(324.68, -27.13) * mm, "end": v(326.14, -22.4) * mm});
            skArc(sketch, "E609", {"start": v(326.14, -22.4) * mm, "mid": v(326.72, -19.93) * mm, "end": v(327.17, -17.43) * mm});
            skArc(sketch, "E610", {"start": v(327.17, -17.43) * mm, "mid": v(327.29, -15.74) * mm, "end": v(327.13, -14.04) * mm});
            skArc(sketch, "E611", {"start": v(327.13, -14.04) * mm, "mid": v(326.76, -12.84) * mm, "end": v(326.1, -11.78) * mm});
            skArc(sketch, "E612", {"start": v(326.1, -11.78) * mm, "mid": v(325.17, -10.92) * mm, "end": v(324.06, -10.32) * mm});
            skArc(sketch, "E613", {"start": v(324.06, -10.32) * mm, "mid": v(323.27, -10.08) * mm, "end": v(322.45, -9.95) * mm});
            skArc(sketch, "E614", {"start": v(322.45, -9.95) * mm, "mid": v(320.6, -9.78) * mm, "end": v(318.74, -9.64) * mm});
            skArc(sketch, "E615", {"start": v(318.74, -9.64) * mm, "mid": v(316.53, -9.52) * mm, "end": v(314.3, -9.43) * mm});
            skArc(sketch, "E616", {"start": v(314.3, -9.43) * mm, "mid": v(311.91, -9.38) * mm, "end": v(309.52, -9.36) * mm});
            skArc(sketch, "E617", {"start": v(309.52, -9.36) * mm, "mid": v(305.57, -9.35) * mm, "end": v(301.6, -9.32) * mm});
            skArc(sketch, "E618", {"start": v(301.6, -9.32) * mm, "mid": v(300.35, -9.25) * mm, "end": v(299.1, -9.07) * mm});
            skArc(sketch, "E619", {"start": v(299.1, -9.07) * mm, "mid": v(298.53, -8.83) * mm, "end": v(298.1, -8.38) * mm});
            skArc(sketch, "E620", {"start": v(298.1, -8.38) * mm, "mid": v(297.86, -7.77) * mm, "end": v(297.84, -7.11) * mm});
            skArc(sketch, "E621", {"start": v(297.84, -7.11) * mm, "mid": v(298.06, -6.41) * mm, "end": v(298.51, -5.83) * mm});
            skArc(sketch, "E622", {"start": v(298.51, -5.83) * mm, "mid": v(299.16, -5.4) * mm, "end": v(299.9, -5.16) * mm});
            skArc(sketch, "E623", {"start": v(299.9, -5.16) * mm, "mid": v(301.38, -4.97) * mm, "end": v(302.88, -4.9) * mm});
            skArc(sketch, "E624", {"start": v(302.88, -4.9) * mm, "mid": v(307.27, -4.87) * mm, "end": v(311.66, -4.86) * mm});
            skArc(sketch, "E625", {"start": v(311.66, -4.86) * mm, "mid": v(314.32, -4.88) * mm, "end": v(317, -4.92) * mm});
            skArc(sketch, "E626", {"start": v(317, -4.92) * mm, "mid": v(319.42, -5) * mm, "end": v(321.85, -5.1) * mm});
            skArc(sketch, "E627", {"start": v(321.85, -5.1) * mm, "mid": v(323.88, -5.22) * mm, "end": v(325.9, -5.36) * mm});
            skArc(sketch, "E628", {"start": v(325.9, -5.36) * mm, "mid": v(326.67, -5.47) * mm, "end": v(327.4, -5.68) * mm});
            skArc(sketch, "E629", {"start": v(327.4, -5.68) * mm, "mid": v(328.05, -5.87) * mm, "end": v(328.71, -6) * mm});
            skArc(sketch, "E630", {"start": v(328.71, -6) * mm, "mid": v(329.06, -5.95) * mm, "end": v(329.33, -5.7) * mm});
            skArc(sketch, "E631", {"start": v(329.33, -5.7) * mm, "mid": v(329.53, -5.25) * mm, "end": v(329.6, -4.76) * mm});
            skArc(sketch, "E632", {"start": v(329.6, -4.76) * mm, "mid": v(329.64, -3.35) * mm, "end": v(329.66, -1.93) * mm});
            skLineSegment(sketch, "E633", {"start": v(329.66, -1.93) * mm, "end": v(329.66, 2.64) * mm});
            skLineSegment(sketch, "E634", {"start": v(329.66, 2.64) * mm, "end": v(308.9, 2.64) * mm});
            skArc(sketch, "E635", {"start": v(308.9, 2.64) * mm, "mid": v(302.92, 2.62) * mm, "end": v(296.94, 2.58) * mm});
            skArc(sketch, "E636", {"start": v(296.94, 2.58) * mm, "mid": v(294.04, 2.5) * mm, "end": v(291.14, 2.32) * mm});
            skArc(sketch, "E637", {"start": v(291.14, 2.32) * mm, "mid": v(289.37, 2.12) * mm, "end": v(287.63, 1.8) * mm});
            skArc(sketch, "E638", {"start": v(287.63, 1.8) * mm, "mid": v(286.35, 1.4) * mm, "end": v(285.16, 0.8) * mm});
            skArc(sketch, "E639", {"start": v(342.54, 1.14) * mm, "mid": v(341.96, 0.78) * mm, "end": v(341.42, 0.36) * mm});
            skArc(sketch, "E640", {"start": v(341.42, 0.36) * mm, "mid": v(340.8, -0.22) * mm, "end": v(340.23, -0.83) * mm});
            skArc(sketch, "E641", {"start": v(340.23, -0.83) * mm, "mid": v(339.67, -1.5) * mm, "end": v(339.15, -2.21) * mm});
            skArc(sketch, "E642", {"start": v(339.15, -2.21) * mm, "mid": v(338.73, -2.88) * mm, "end": v(338.36, -3.57) * mm});
            skArc(sketch, "E643", {"start": v(338.36, -3.57) * mm, "mid": v(337.22, -6.27) * mm, "end": v(336.32, -9.06) * mm});
            skArc(sketch, "E644", {"start": v(336.32, -9.06) * mm, "mid": v(335.12, -13.55) * mm, "end": v(334.02, -18.07) * mm});
            skArc(sketch, "E645", {"start": v(334.02, -18.07) * mm, "mid": v(333.02, -22.57) * mm, "end": v(332.12, -27.1) * mm});
            skArc(sketch, "E646", {"start": v(332.12, -27.1) * mm, "mid": v(331.84, -29.4) * mm, "end": v(331.86, -31.72) * mm});
            skArc(sketch, "E647", {"start": v(331.86, -31.72) * mm, "mid": v(332.27, -33.66) * mm, "end": v(333.2, -35.41) * mm});
            skArc(sketch, "E648", {"start": v(333.2, -35.41) * mm, "mid": v(334.5, -36.67) * mm, "end": v(336.15, -37.4) * mm});
            skArc(sketch, "E649", {"start": v(336.15, -37.4) * mm, "mid": v(339.3, -37.97) * mm, "end": v(342.48, -38.2) * mm});
            skArc(sketch, "E650", {"start": v(342.48, -38.2) * mm, "mid": v(351.14, -38.3) * mm, "end": v(359.8, -38.35) * mm});
            skLineSegment(sketch, "E651", {"start": v(359.8, -38.35) * mm, "end": v(382.44, -38.36) * mm});
            skLineSegment(sketch, "E652", {"start": v(382.44, -38.36) * mm, "end": v(384.05, -34.34) * mm});
            skArc(sketch, "E653", {"start": v(384.05, -34.34) * mm, "mid": v(384.36, -33.56) * mm, "end": v(384.66, -32.78) * mm});
            skArc(sketch, "E654", {"start": v(384.66, -32.78) * mm, "mid": v(384.93, -32.1) * mm, "end": v(385.18, -31.43) * mm});
            skArc(sketch, "E655", {"start": v(385.18, -31.43) * mm, "mid": v(385.4, -30.85) * mm, "end": v(385.63, -30.26) * mm});
            skArc(sketch, "E656", {"start": v(385.63, -30.26) * mm, "mid": v(385.65, -30.18) * mm, "end": v(385.66, -30.1) * mm});
            skArc(sketch, "E657", {"start": v(385.66, -30.1) * mm, "mid": v(385.63, -30.02) * mm, "end": v(385.56, -30) * mm});
            skArc(sketch, "E658", {"start": v(385.56, -30) * mm, "mid": v(383.26, -30.01) * mm, "end": v(380.96, -30.03) * mm});
            skArc(sketch, "E659", {"start": v(380.96, -30.03) * mm, "mid": v(378.38, -30.05) * mm, "end": v(375.8, -30.09) * mm});
            skArc(sketch, "E660", {"start": v(375.8, -30.09) * mm, "mid": v(372.73, -30.14) * mm, "end": v(369.66, -30.2) * mm});
            skArc(sketch, "E661", {"start": v(369.66, -30.2) * mm, "mid": v(363.88, -30.3) * mm, "end": v(358.1, -30.33) * mm});
            skArc(sketch, "E662", {"start": v(358.1, -30.33) * mm, "mid": v(356.18, -30.19) * mm, "end": v(354.3, -29.74) * mm});
            skArc(sketch, "E663", {"start": v(354.3, -29.74) * mm, "mid": v(353.37, -29.12) * mm, "end": v(352.9, -28.1) * mm});
            skArc(sketch, "E664", {"start": v(352.9, -28.1) * mm, "mid": v(352.83, -26.47) * mm, "end": v(353.07, -24.86) * mm});
            skLineSegment(sketch, "E665", {"start": v(353.07, -24.86) * mm, "end": v(353.7, -22.36) * mm});
            skLineSegment(sketch, "E666", {"start": v(353.7, -22.36) * mm, "end": v(371.14, -22.36) * mm});
            skLineSegment(sketch, "E667", {"start": v(371.14, -22.36) * mm, "end": v(388.58, -22.36) * mm});
            skLineSegment(sketch, "E668", {"start": v(388.58, -22.36) * mm, "end": v(389.57, -18.61) * mm});
            skArc(sketch, "E669", {"start": v(389.57, -18.61) * mm, "mid": v(390.71, -14.16) * mm, "end": v(391.79, -9.7) * mm});
            skArc(sketch, "E670", {"start": v(391.79, -9.7) * mm, "mid": v(392.24, -7.3) * mm, "end": v(392.48, -4.88) * mm});
            skArc(sketch, "E671", {"start": v(392.48, -4.88) * mm, "mid": v(392.43, -3.3) * mm, "end": v(392.1, -1.76) * mm});
            skArc(sketch, "E672", {"start": v(392.1, -1.76) * mm, "mid": v(391.53, -0.47) * mm, "end": v(390.66, 0.64) * mm});
            skArc(sketch, "E673", {"start": v(390.66, 0.64) * mm, "mid": v(389.77, 1.33) * mm, "end": v(388.74, 1.78) * mm});
            skArc(sketch, "E674", {"start": v(388.74, 1.78) * mm, "mid": v(387.26, 2.14) * mm, "end": v(385.74, 2.34) * mm});
            skArc(sketch, "E675", {"start": v(385.74, 2.34) * mm, "mid": v(383.04, 2.5) * mm, "end": v(380.32, 2.58) * mm});
            skArc(sketch, "E676", {"start": v(380.32, 2.58) * mm, "mid": v(373.61, 2.6) * mm, "end": v(366.9, 2.6) * mm});
            skArc(sketch, "E677", {"start": v(366.9, 2.6) * mm, "mid": v(361.39, 2.57) * mm, "end": v(355.87, 2.52) * mm});
            skArc(sketch, "E678", {"start": v(355.87, 2.52) * mm, "mid": v(352.51, 2.43) * mm, "end": v(349.16, 2.27) * mm});
            skArc(sketch, "E679", {"start": v(349.16, 2.27) * mm, "mid": v(346.97, 2.1) * mm, "end": v(344.78, 1.86) * mm});
            skArc(sketch, "E680", {"start": v(344.78, 1.86) * mm, "mid": v(343.62, 1.6) * mm, "end": v(342.54, 1.14) * mm});
            skArc(sketch, "E681", {"start": v(371.33, -5.44) * mm, "mid": v(371.59, -5.77) * mm, "end": v(371.75, -6.15) * mm});
            skArc(sketch, "E682", {"start": v(371.75, -6.15) * mm, "mid": v(371.87, -6.67) * mm, "end": v(371.9, -7.2) * mm});
            skArc(sketch, "E683", {"start": v(371.9, -7.2) * mm, "mid": v(371.89, -7.9) * mm, "end": v(371.8, -8.6) * mm});
            skArc(sketch, "E684", {"start": v(371.8, -8.6) * mm, "mid": v(371.62, -9.52) * mm, "end": v(371.4, -10.44) * mm});
            skLineSegment(sketch, "E685", {"start": v(371.4, -10.44) * mm, "end": v(370.41, -14.36) * mm});
            skLineSegment(sketch, "E686", {"start": v(370.41, -14.36) * mm, "end": v(362.93, -14.36) * mm});
            skArc(sketch, "E687", {"start": v(362.93, -14.36) * mm, "mid": v(360.84, -14.35) * mm, "end": v(358.74, -14.31) * mm});
            skArc(sketch, "E688", {"start": v(358.74, -14.31) * mm, "mid": v(357.81, -14.24) * mm, "end": v(356.89, -14.08) * mm});
            skArc(sketch, "E689", {"start": v(356.89, -14.08) * mm, "mid": v(356.47, -13.9) * mm, "end": v(356.14, -13.57) * mm});
            skArc(sketch, "E690", {"start": v(356.14, -13.57) * mm, "mid": v(356, -13.19) * mm, "end": v(356.05, -12.78) * mm});
            skArc(sketch, "E691", {"start": v(356.05, -12.78) * mm, "mid": v(356.17, -12.43) * mm, "end": v(356.28, -12.07) * mm});
            skArc(sketch, "E692", {"start": v(356.28, -12.07) * mm, "mid": v(356.39, -11.66) * mm, "end": v(356.48, -11.24) * mm});
            skArc(sketch, "E693", {"start": v(356.48, -11.24) * mm, "mid": v(356.55, -10.84) * mm, "end": v(356.61, -10.44) * mm});
            skArc(sketch, "E694", {"start": v(356.61, -10.44) * mm, "mid": v(356.65, -10.1) * mm, "end": v(356.66, -9.78) * mm});
            skArc(sketch, "E695", {"start": v(356.66, -9.78) * mm, "mid": v(356.83, -8.68) * mm, "end": v(357.32, -7.68) * mm});
            skArc(sketch, "E696", {"start": v(357.32, -7.68) * mm, "mid": v(358.17, -6.7) * mm, "end": v(359.2, -5.93) * mm});
            skArc(sketch, "E697", {"start": v(359.2, -5.93) * mm, "mid": v(360.57, -5.23) * mm, "end": v(362.04, -4.76) * mm});
            skArc(sketch, "E698", {"start": v(362.04, -4.76) * mm, "mid": v(363.74, -4.46) * mm, "end": v(365.46, -4.36) * mm});
            skArc(sketch, "E699", {"start": v(365.46, -4.36) * mm, "mid": v(366.42, -4.38) * mm, "end": v(367.37, -4.44) * mm});
            skArc(sketch, "E700", {"start": v(367.37, -4.44) * mm, "mid": v(368.27, -4.54) * mm, "end": v(369.16, -4.68) * mm});
            skArc(sketch, "E701", {"start": v(369.16, -4.68) * mm, "mid": v(369.9, -4.83) * mm, "end": v(370.62, -5.02) * mm});
            skArc(sketch, "E702", {"start": v(370.62, -5.02) * mm, "mid": v(371, -5.18) * mm, "end": v(371.33, -5.44) * mm});
            skSolve(sketch);
        }
        {
            var Q0;
            Q0=makeQuery(id+"F3.imprint","IMPRINT",FACE,{"disambiguationData":[TD([[makeQuery(id+"F3.imprint","IMPRINT",EDGE,{"derivedFrom":sQuery(id+"F3.wireOp",EDGE,"E1")}),-1.0]])]});
            extrude(context, id + "F4", {"entities" : qUnion([Q0]), "operationType" : NewBodyOperationType.REMOVE, "oppositeDirection" : true, "depth" : 26 * mm});
        }
    });
